FCSTD DOCUMENT  (FreeCAD 0.20R29410 (Git))
Label: copter
License: All rights reserved
LicenseURL: http://en.wikipedia.org/wiki/All_rights_reserved
objects: App::Link×23, App::DocumentObjectGroup×3, PartDesign::CoordinateSystem×1, App::FeaturePython×1, App::Part×1
note: 1 computed .brp shape members not serialized (recipe doc carries the construction recipe); baked Part::Feature solids carry a one-line shape summary decoded from their .brp
EXTERNAL_REF file=lower_plate.FCStd obj=LCS_1
EXTERNAL_REF file=lower_plate.FCStd obj=Body
EXTERNAL_REF file=arm.FCStd obj=LCS_IR
EXTERNAL_REF file=lower_plate.FCStd obj=LCS_7
EXTERNAL_REF file=arm.FCStd obj=Body
EXTERNAL_REF file=arm.FCStd obj=LCS_IL
EXTERNAL_REF file=lower_plate.FCStd obj=LCS_6
EXTERNAL_REF file=lower_plate.FCStd obj=LCS_2
EXTERNAL_REF file=lower_plate.FCStd obj=LCS_3
EXTERNAL_REF file=arm.FCStd obj=LCS_1
EXTERNAL_REF file=motor_1810.FCStd obj=LCS_1
EXTERNAL_REF file=motor_1810.FCStd obj=Body
EXTERNAL_REF file=arm.FCStd obj=LCS_R
EXTERNAL_REF file=middle_plate.FCStd obj=LCS_1
EXTERNAL_REF file=middle_plate.FCStd obj=Body
EXTERNAL_REF file=back_pillar.FCStd obj=LCS_1
EXTERNAL_REF file=lower_plate.FCStd obj=LCS_4
EXTERNAL_REF file=back_pillar.FCStd obj=Body
EXTERNAL_REF file=lower_plate.FCStd obj=LCS_5
EXTERNAL_REF file=back_pillar.FCStd obj=LCS_2
EXTERNAL_REF file=top_plate.FCStd obj=LCS_2
EXTERNAL_REF file=top_plate.FCStd obj=Body
EXTERNAL_REF file=front_pillar.FCStd obj=LCS_1
EXTERNAL_REF file=middle_plate.FCStd obj=LCS_2
EXTERNAL_REF file=front_pillar.FCStd obj=Body
EXTERNAL_REF file=middle_plate.FCStd obj=LCS_3
EXTERNAL_REF file=prop.FCStd obj=Body
EXTERNAL_REF file=prop1.FCStd obj=Body001
EXTERNAL_REF file=lower_plate.FCStd obj=LCS_8
EXTERNAL_REF file=lower_plate.FCStd obj=LCS_9
EXTERNAL_REF file=middle_plate.FCStd obj=LCS_4
EXTERNAL_REF file=middle_plate.FCStd obj=LCS_5

FEATURE [App::DocumentObjectGroup] Parts
FEATURE [PartDesign::CoordinateSystem] LCS_Origin
  AttacherType = Attacher::AttachEngine3D
  MapMode = 2
  Support = -> [X_Axis]
FEATURE [App::DocumentObjectGroup] Constraints
FEATURE [App::FeaturePython] Variables  # WARN: FeaturePython — macro-defined, semantics opaque (R4)
  Type = App::PropertyContainer
  angle = 720
  minus_angle = 180
FEATURE [App::DocumentObjectGroup] Configurations
FEATURE [App::Link] Body  label="LowerPlate"
  AssemblyType = Part::Link
  AttachedBy = #LCS_1
  AttachedTo = Parent Assembly#LCS_Origin
  LinkPlacement = pos=(-17.5,100,0) rot=(0,0,1;0rad)
  LinkedObject = -> <external lower_plate.FCStd>#Body
  Placement = pos=(-17.5,100,0) rot=(0,0,1;0rad)
  SolverId = Asm4EE
  expr: Placement = LCS_Origin.Placement * AttachmentOffset * lower_plate#LCS_1.Placement ^ -1
FEATURE [App::Link] Body001  label="Arm1"
  AssemblyType = Part::Link
  AttachedBy = #LCS_IR
  AttachedTo = Body#LCS_7
  LinkPlacement = pos=(-17.75,100.25,2) rot=(0,0,1;0rad)
  LinkedObject = -> <external arm.FCStd>#Body
  Placement = pos=(-17.75,100.25,2) rot=(0,0,1;0rad)
  SolverId = Asm4EE
  expr: Placement = Body.Placement * lower_plate#LCS_7.Placement * AttachmentOffset * arm#LCS_IR.Placement ^ -1
FEATURE [App::Link] Body_2  label="Arm4"
  AssemblyType = Part::Link
  AttachedBy = #LCS_IL
  AttachedTo = Body#LCS_6
  AttachmentOffset = pos=(0,0,0) rot=(1,0,0;3.14159rad)
  LinkPlacement = pos=(-17.25,100.25,6) rot=(0,1,0;3.14159rad)
  LinkedObject = -> <external arm.FCStd>#Body
  Placement = pos=(-17.25,100.25,6) rot=(0,1,0;3.14159rad)
  SolverId = Asm4EE
  expr: Placement = Body.Placement * lower_plate#LCS_6.Placement * AttachmentOffset * arm#LCS_IL.Placement ^ -1
FEATURE [App::Link] Body002  label="Arm2"
  AssemblyType = Part::Link
  AttachedBy = #LCS_IL
  AttachedTo = Body#LCS_2
  AttachmentOffset = pos=(0,0,0) rot=(0,1,0;3.14159rad)
  LinkPlacement = pos=(-17.75,99.75,6) rot=(-1,0,0;3.14159rad)
  LinkedObject = -> <external arm.FCStd>#Body
  Placement = pos=(-17.75,99.75,6) rot=(-1,0,0;3.14159rad)
  SolverId = Asm4EE
  expr: Placement = Body.Placement * lower_plate#LCS_2.Placement * AttachmentOffset * arm#LCS_IL.Placement ^ -1
FEATURE [App::Link] Body003  label="Arm3"
  AssemblyType = Part::Link
  AttachedBy = #LCS_IR
  AttachedTo = Body#LCS_3
  AttachmentOffset = pos=(0,0,0) rot=(0,0,1;3.14159rad)
  LinkPlacement = pos=(-17.25,99.75,2) rot=(0,0,1;3.14159rad)
  LinkedObject = -> <external arm.FCStd>#Body
  Placement = pos=(-17.25,99.75,2) rot=(0,0,1;3.14159rad)
  SolverId = Asm4EE
  expr: Placement = Body.Placement * lower_plate#LCS_3.Placement * AttachmentOffset * arm#LCS_IR.Placement ^ -1
FEATURE [App::Link] Body004  label="Motor1"
  AssemblyType = Part::Link
  AttachedBy = #LCS_1
  AttachedTo = Body001#LCS_1
  AttachmentOffset = pos=(0,0,0) rot=(1,0,0;3.14159rad)
  LinkPlacement = pos=(-113.703,173.838,6) rot=(0,0,1;4.01426rad)
  LinkedObject = -> <external motor_1810.FCStd>#Body
  Placement = pos=(-113.703,173.838,6) rot=(0,0,1;4.01426rad)
  SolverId = Asm4EE
  expr: .Placement.Rotation.Angle = 230
  expr: Placement = Body001.Placement * arm#LCS_1.Placement * AttachmentOffset * motor_1810#LCS_1.Placement ^ -1
FEATURE [App::Link] Body006  label="Motor2"
  AssemblyType = Part::Link
  AttachedBy = #LCS_1
  AttachedTo = Body002#LCS_R
  LinkPlacement = pos=(-113.703,26.162,6) rot=(0,0,1;5.41052rad)
  LinkedObject = -> <external motor_1810.FCStd>#Body
  Placement = pos=(-113.703,26.162,6) rot=(0,0,1;5.41052rad)
  SolverId = Asm4EE
  expr: .Placement.Rotation.Angle = 300
  expr: Placement = Body002.Placement * arm#LCS_R.Placement * AttachmentOffset * motor_1810#LCS_1.Placement ^ -1
FEATURE [App::Link] Body007  label="Motor3"
  AssemblyType = Part::Link
  AttachedBy = #LCS_1
  AttachedTo = Body003#LCS_1
  AttachmentOffset = pos=(0,0,0) rot=(1,0,0;3.14159rad)
  LinkPlacement = pos=(78.703,26.162,6) rot=(0,0,-1;5.41052rad)
  LinkedObject = -> <external motor_1810.FCStd>#Body
  Placement = pos=(78.703,26.162,6) rot=(0,0,-1;5.41052rad)
  SolverId = Asm4EE
  expr: .Placement.Rotation.Angle = 60
  expr: Placement = Body003.Placement * arm#LCS_1.Placement * AttachmentOffset * motor_1810#LCS_1.Placement ^ -1
FEATURE [App::Link] Body008  label="Motor4"
  AssemblyType = Part::Link
  AttachedBy = #LCS_1
  AttachedTo = Body_2#LCS_R
  LinkPlacement = pos=(78.703,173.838,6) rot=(0,0,1;2.26893rad)
  LinkedObject = -> <external motor_1810.FCStd>#Body
  Placement = pos=(78.703,173.838,6) rot=(0,0,1;2.26893rad)
  SolverId = Asm4EE
  expr: .Placement.Rotation.Angle = 120
  expr: Placement = Body_2.Placement * arm#LCS_R.Placement * AttachmentOffset * motor_1810#LCS_1.Placement ^ -1
FEATURE [App::Link] Body001006  label="MiddlePlate"
  AssemblyType = Part::Link
  AttachedBy = #LCS_1
  AttachedTo = Body_2#LCS_IR
  AttachmentOffset = pos=(0,0,0) rot=(1,0,0;3.14159rad)
  LinkPlacement = pos=(-17.5,100,6) rot=(0,0,1;0rad)
  LinkedObject = -> <external middle_plate.FCStd>#Body
  Placement = pos=(-17.5,100,6) rot=(0,0,1;0rad)
  SolverId = Asm4EE
  expr: Placement = Body_2.Placement * arm#LCS_IR.Placement * AttachmentOffset * middle_plate#LCS_1.Placement ^ -1
FEATURE [App::Link] Body001007  label="BackPillarLeft"
  AssemblyType = Part::Link
  AttachedBy = #LCS_1
  AttachedTo = Body#LCS_4
  LinkPlacement = pos=(-31,4,2) rot=(0,0,1;0rad)
  LinkedObject = -> <external back_pillar.FCStd>#Body
  Placement = pos=(-31,4,2) rot=(0,0,1;0rad)
  SolverId = Asm4EE
  expr: Placement = Body.Placement * lower_plate#LCS_4.Placement * AttachmentOffset * back_pillar#LCS_1.Placement ^ -1
FEATURE [App::Link] Body001008  label="BackPillarRight"
  AssemblyType = Part::Link
  AttachedBy = #LCS_1
  AttachedTo = Body#LCS_5
  LinkPlacement = pos=(-4,4,2) rot=(0,0,1;0rad)
  LinkedObject = -> <external back_pillar.FCStd>#Body
  Placement = pos=(-4,4,2) rot=(0,0,1;0rad)
  SolverId = Asm4EE
  expr: Placement = Body.Placement * lower_plate#LCS_5.Placement * AttachmentOffset * back_pillar#LCS_1.Placement ^ -1
FEATURE [App::Link] Body001009  label="TopPlate"
  AssemblyType = Part::Link
  AttachedBy = #LCS_2
  AttachedTo = Body001007#LCS_2
  AttachmentOffset = pos=(0,0,0) rot=(0,0,1;3.14159rad)
  LinkPlacement = pos=(-17.5,100,37) rot=(0,0,1;3.14159rad)
  LinkedObject = -> <external top_plate.FCStd>#Body
  Placement = pos=(-17.5,100,37) rot=(0,0,1;3.14159rad)
  SolverId = Asm4EE
  expr: Placement = Body001007.Placement * back_pillar#LCS_2.Placement * AttachmentOffset * top_plate#LCS_2.Placement ^ -1
FEATURE [App::Link] Body001010  label="FrontPillarLeft"
  AssemblyType = Part::Link
  AttachedBy = #LCS_1
  AttachedTo = Body001006#LCS_2
  LinkPlacement = pos=(-31,196,8) rot=(0,0,1;0rad)
  LinkedObject = -> <external front_pillar.FCStd>#Body
  Placement = pos=(-31,196,8) rot=(0,0,1;0rad)
  SolverId = Asm4EE
  expr: Placement = Body001006.Placement * middle_plate#LCS_2.Placement * AttachmentOffset * front_pillar#LCS_1.Placement ^ -1
FEATURE [App::Link] Body001011  label="FrontPillarRight"
  AssemblyType = Part::Link
  AttachedBy = #LCS_1
  AttachedTo = Body001006#LCS_3
  LinkPlacement = pos=(-4,196,8) rot=(0,0,1;0rad)
  LinkedObject = -> <external front_pillar.FCStd>#Body
  Placement = pos=(-4,196,8) rot=(0,0,1;0rad)
  SolverId = Asm4EE
  expr: Placement = Body001006.Placement * middle_plate#LCS_3.Placement * AttachmentOffset * front_pillar#LCS_1.Placement ^ -1
FEATURE [App::Link] Body001012  label="Prop1"
  AssemblyType = Part::Link
  AttachedBy = #LCS_1
  AttachedTo = Body004#LCS_2
  AttachmentOffset = pos=(0,0,0) rot=(1,0,0;3.14159rad)
  LinkPlacement = pos=(-113.453,173.588,27.3) rot=(0,0,1;12.5664rad)
  LinkedObject = -> <external prop.FCStd>#Body
  Placement = pos=(-113.453,173.588,27.3) rot=(0,0,1;12.5664rad)
  SolverId = Asm4EE
  expr: .Placement.Rotation.Angle = Variables.angle
FEATURE [App::Link] Body001013  label="Prop2"
  AssemblyType = Part::Link
  AttachedBy = #LCS_2
  AttachedTo = Body006#LCS_2
  AttachmentOffset = pos=(0,0,0) rot=(0,0,1;3.14159rad)
  LinkPlacement = pos=(-113.453,26.412,27.3) rot=(0,0,1;-12.5664rad)
  LinkedObject = -> <external prop1.FCStd>#Body001
  Placement = pos=(-113.453,26.412,27.3) rot=(0,0,1;-12.5664rad)
  SolverId = Asm4EE
  expr: .Placement.Rotation.Angle = -Variables.angle
FEATURE [App::Link] Body001014  label="Prop3"
  AssemblyType = Part::Link
  AttachedBy = #LCS_1
  AttachedTo = Body007#LCS_2
  AttachmentOffset = pos=(0,0,0) rot=(0.707107,-0.707107,0;3.14159rad)
  LinkPlacement = pos=(78.453,26.412,27.3) rot=(0,0,1;12.5664rad)
  LinkedObject = -> <external prop.FCStd>#Body
  Placement = pos=(78.453,26.412,27.3) rot=(0,0,1;12.5664rad)
  SolverId = Asm4EE
  expr: .Placement.Rotation.Angle = Variables.angle
FEATURE [App::Link] Body001015  label="Prop4"
  AssemblyType = Part::Link
  AttachedBy = #LCS_2
  AttachedTo = Body008#LCS_2
  AttachmentOffset = pos=(0,0,0) rot=(0,0,1;3.14159rad)
  LinkPlacement = pos=(78.453,173.588,27.3) rot=(0,0,1;-12.5664rad)
  LinkedObject = -> <external prop1.FCStd>#Body001
  Placement = pos=(78.453,173.588,27.3) rot=(0,0,1;-12.5664rad)
  SolverId = Asm4EE
  expr: .Placement.Rotation.Angle = -Variables.angle
FEATURE [App::Link] Body001016  label="BackPIllarMidLeft"
  AssemblyType = Part::Link
  AttachedBy = #LCS_1
  AttachedTo = Body#LCS_8
  LinkPlacement = pos=(-31,70,2) rot=(0,0,1;0rad)
  LinkedObject = -> <external back_pillar.FCStd>#Body
  Placement = pos=(-31,70,2) rot=(0,0,1;0rad)
  SolverId = Asm4EE
  expr: Placement = Body.Placement * lower_plate#LCS_8.Placement * AttachmentOffset * back_pillar#LCS_1.Placement ^ -1
FEATURE [App::Link] Body001017  label="BackPillarMiddleRight"
  AssemblyType = Part::Link
  AttachedBy = #LCS_1
  AttachedTo = Body#LCS_9
  LinkPlacement = pos=(-4,70,2) rot=(0,0,1;0rad)
  LinkedObject = -> <external back_pillar.FCStd>#Body
  Placement = pos=(-4,70,2) rot=(0,0,1;0rad)
  SolverId = Asm4EE
  expr: Placement = Body.Placement * lower_plate#LCS_9.Placement * AttachmentOffset * back_pillar#LCS_1.Placement ^ -1
FEATURE [App::Link] Body001018  label="FrontPillarMidLeft"
  AssemblyType = Part::Link
  AttachedBy = #LCS_1
  AttachedTo = Body001006#LCS_4
  LinkPlacement = pos=(-31,140,8) rot=(0,0,1;0rad)
  LinkedObject = -> <external front_pillar.FCStd>#Body
  Placement = pos=(-31,140,8) rot=(0,0,1;0rad)
  SolverId = Asm4EE
  expr: Placement = Body001006.Placement * middle_plate#LCS_4.Placement * AttachmentOffset * front_pillar#LCS_1.Placement ^ -1
FEATURE [App::Link] Body_3  label="FronPillarMidRight"
  AssemblyType = Part::Link
  AttachedBy = #LCS_1
  AttachedTo = Body001006#LCS_5
  LinkPlacement = pos=(-4,140,8) rot=(0,0,1;0rad)
  LinkedObject = -> <external front_pillar.FCStd>#Body
  Placement = pos=(-4,140,8) rot=(0,0,1;0rad)
  SolverId = Asm4EE
  expr: Placement = Body001006.Placement * middle_plate#LCS_5.Placement * AttachmentOffset * front_pillar#LCS_1.Placement ^ -1
FEATURE [App::Part] Model
  AssemblyType = Part::Link
  Group = -> [LCS_Origin,Constraints,Variables,Configurations,Body,Body001,Body_2,Body002,Body003,Body004,Body006,Body007,Body008,Body001006,Body001007,Body001008,Body001009,Body001010,Body001011,Body001012,Body001013,Body001014,Body001015,Body001016,Body001017,Body001018,Body_3]
  Origin = -> Origin
  Type = Assembly

RESOLVED EXTERNAL PARTS (link-assembly join: the EXTERNAL_REF files above that resolve inside this repo's crawl, each included once):
---- part arm.FCStd = doc fcstd_1915403416bb ----
FCSTD DOCUMENT  (FreeCAD 0.20R29410 (Git))
Label: arm
License: All rights reserved
LicenseURL: http://en.wikipedia.org/wiki/All_rights_reserved
objects: PartDesign::CoordinateSystem×4, Sketcher::SketchObject×1, PartDesign::Pad×1, PartDesign::Body×1
note: 8 computed .brp shape members not serialized (recipe doc carries the construction recipe); baked Part::Feature solids carry a one-line shape summary decoded from their .brp

FEATURE [Sketcher::SketchObject] Sketch
  FullyConstrained = true
  MapMode = 5
  Support = -> [XY_Plane]
  sketch-geometry (22):
    g0: LineSegment StartX=-20 StartY=0 StartZ=0 EndX=0 EndY=0 EndZ=0
    g1: LineSegment StartX=0 StartY=0 StartZ=0 EndX=0 EndY=15 EndZ=0
    g2: LineSegment StartX=-20 StartY=0 StartZ=0 EndX=-96.6044 EndY=64.2788 EndZ=0
    g3: LineSegment StartX=0 StartY=15 StartZ=0 EndX=-86.8979 EndY=75.8466 EndZ=0
    g4: LineSegment StartX=-96.6044 StartY=64.2788 StartZ=0 EndX=-86.8979 EndY=75.8466 EndZ=0
    g5: LineSegment StartX=-91.7514 StartY=70.0624 StartZ=0 EndX=-95.0006 EndY=78.9895 EndZ=0
    g6: LineSegment StartX=-95.0006 StartY=78.9895 StartZ=0 EndX=-101.107 EndY=71.7121 EndZ=0
    g7: LineSegment StartX=-101.107 StartY=71.7121 StartZ=0 EndX=-91.7514 EndY=70.0624 EndZ=0
    g8: Circle CenterX=-95.953 CenterY=73.588 CenterZ=0 NormalX=0 NormalY=0 NormalZ=1 AngleXU=0 Radius=5.48483
    g9: Circle CenterX=-91.7514 CenterY=70.0624 CenterZ=0 NormalX=0 NormalY=0 NormalZ=1 AngleXU=0 Radius=1.1
    g10: Circle CenterX=-95.0006 CenterY=78.9895 CenterZ=0 NormalX=0 NormalY=0 NormalZ=1 AngleXU=0 Radius=1.1
    g11: Circle CenterX=-101.107 CenterY=71.7121 CenterZ=0 NormalX=0 NormalY=0 NormalZ=1 AngleXU=0 Radius=1.1
    g12: ArcOfCircle CenterX=-95.953 CenterY=73.588 CenterZ=0 NormalX=0 NormalY=0 NormalZ=1 AngleXU=0 Radius=3.75 StartAngle=1.79996 EndAngle=3.08696
    g13: ArcOfCircle CenterX=-95.0006 CenterY=78.9895 CenterZ=0 NormalX=0 NormalY=0 NormalZ=1 AngleXU=0 Radius=2 StartAngle=0.311549 EndAngle=3.45314
    g14: ArcOfCircle CenterX=-101.107 CenterY=71.7121 CenterZ=0 NormalX=0 NormalY=0 NormalZ=1 AngleXU=0 Radius=2 StartAngle=1.43378 EndAngle=4.57537
    g15: LineSegment StartX=-96.8049 StartY=77.2399 StartZ=0 EndX=-96.9043 EndY=78.3764 EndZ=0
    g16: LineSegment StartX=-99.6974 StartY=73.7927 StartZ=0 EndX=-100.834 EndY=73.6933 EndZ=0
    g17: LineSegment StartX=-99.6974 StartY=73.7927 StartZ=0 EndX=-96.8049 EndY=77.2399 EndZ=0
    g18: LineSegment StartX=-86.8979 StartY=75.8466 StartZ=0 EndX=-93.0969 EndY=79.6025 EndZ=0
    g19: LineSegment StartX=-96.6044 StartY=64.2788 StartZ=0 EndX=-101.38 EndY=69.7308 EndZ=0
    g20: Circle CenterX=-95.953 CenterY=73.588 CenterZ=0 NormalX=0 NormalY=0 NormalZ=1 AngleXU=0 Radius=2.25
    g21: Circle CenterX=-15 CenterY=15 CenterZ=0 NormalX=0 NormalY=0 NormalZ=1 AngleXU=0 Radius=1.55
  constraints (59):
    c: PointOnObject(g0,g-1)
    c: Coincident(g0,g-1)
    c: Coincident(g1,g0)
    c: PointOnObject(g1,g-2)
    c: Coincident(g2,g0)
    c: Coincident(g3,g1)
    c: DistanceY(g1,g1) = 15
    c: DistanceX(g0,g0) = 20
    c: Angle(g-1,g2) = 2.44346
    c: Coincident(g4,g2)
    c: Coincident(g4,g3)
    c: Angle(g2,g4) = 1.5708
    c: Angle(g2,g3) = 0.0872665
    c: Distance(g2) = 100
    c: Coincident(g5,g6)
    c: Coincident(g6,g7)
    c: Coincident(g7,g5)
    c: Equal(g5,g6)
    c: Equal(g5,g7)
    c: PointOnObject(g5,g8)
    c: PointOnObject(g6,g8)
    c: PointOnObject(g7,g8)
    c: PointOnObject(g5,g4)
    c: Parallel(g6,g4)
    c: Distance(g5,g2) = 7.55
    c: Coincident(g9,g5)
    c: Coincident(g10,g5)
    c: Coincident(g11,g6)
    c: Equal(g10,g11)
    c: Equal(g10,g9)
    c: Diameter(g10) = 2.2
    c: Distance(g7) = 9.5
    c: Coincident(g12,g8)
    c: Diameter(g12) = 7.5
    c: Coincident(g13,g10)
    c: Coincident(g14,g11)
    c: Diameter(g14) = 4
    c: Diameter(g13) = 4
    c: Angle(g14) = 3.14159
    c: Angle(g13) = 3.14159
    c: Coincident(g15,g12)
    c: Coincident(g15,g13)
    c: Coincident(g16,g12)
    c: Coincident(g16,g14)
    c: Angle(g15,g16) = 1.5708
    c: Equal(g16,g15)
    c: Coincident(g17,g12)
    c: Coincident(g17,g12)
    c: Parallel(g17,g4)
    c: Distance(g17) = 4.5
    c: Coincident(g18,g3)
    c: Coincident(g18,g13)
    c: Coincident(g19,g2)
    c: Coincident(g19,g14)
    c: Coincident(g20,g12)
    c: Diameter(g20) = 4.5
    c: Diameter(g21) = 3.1
    c: DistanceX(g21,g0) = 15
    c: DistanceY(g0,g21) = 15
FEATURE [PartDesign::Pad] Pad
  Direction = (0,0,1)
  Length = 4
  Length2 = 10
  Profile = -> Sketch
  ReferenceAxis = -> Sketch [N_Axis]
  Type = 0
FEATURE [PartDesign::CoordinateSystem] LCS_1  label="LCS_L"
  AttacherType = Attacher::AttachEngine3D
  AttachmentOffset = pos=(0,0,0) rot=(0,0,1;0.872665rad)
  MapMode = 11
  Placement = pos=(-95.953,73.588,4) rot=(0,0,1;2.44346rad)
  Support = -> [Pad]
FEATURE [PartDesign::CoordinateSystem] LCS_R
  AttacherType = Attacher::AttachEngine3D
  AttachmentOffset = pos=(0,0,0) rot=(0,0,1;0.872665rad)
  MapMode = 11
  Placement = pos=(-95.953,73.588,0) rot=(0,0,1;2.44346rad)
  Support = -> [Pad]
FEATURE [PartDesign::CoordinateSystem] LCS_IL
  AttacherType = Attacher::AttachEngine3D
  MapMode = 11
  Placement = pos=(-15,15,4) rot=(0,0,1;1.5708rad)
  Support = -> [Pad]
FEATURE [PartDesign::CoordinateSystem] LCS_IR
  AttacherType = Attacher::AttachEngine3D
  MapMode = 11
  Placement = pos=(-15,15,0) rot=(0,0,1;1.5708rad)
  Support = -> [Pad]
FEATURE [PartDesign::Body] Body
  Group = -> [Sketch,Pad,LCS_1,LCS_R,LCS_IL,LCS_IR]
  Origin = -> Origin
  Tip = -> Pad
---- part back_pillar.FCStd = doc fcstd_aa81737c5687 ----
FCSTD DOCUMENT  (FreeCAD 0.20R29410 (Git))
Label: back_pillar
License: All rights reserved
LicenseURL: http://en.wikipedia.org/wiki/All_rights_reserved
objects: PartDesign::CoordinateSystem×2, Sketcher::SketchObject×1, PartDesign::Pad×1, PartDesign::Body×1
note: 6 computed .brp shape members not serialized (recipe doc carries the construction recipe); baked Part::Feature solids carry a one-line shape summary decoded from their .brp

FEATURE [Sketcher::SketchObject] Sketch
  FullyConstrained = true
  MapMode = 5
  Support = -> [XY_Plane]
  sketch-geometry (2):
    g0: Circle CenterX=0 CenterY=0 CenterZ=0 NormalX=0 NormalY=0 NormalZ=1 AngleXU=0 Radius=2.5
    g1: Circle CenterX=0 CenterY=0 CenterZ=0 NormalX=0 NormalY=0 NormalZ=1 AngleXU=0 Radius=1.5
  constraints (4):
    c: Coincident(g0,g-1)
    c: Coincident(g1,g0)
    c: Diameter(g0) = 5
    c: Diameter(g1) = 3
FEATURE [PartDesign::Pad] Pad
  Direction = (0,0,1)
  Length = 35
  Length2 = 10
  Profile = -> Sketch
  ReferenceAxis = -> Sketch [N_Axis]
  Type = 0
FEATURE [PartDesign::CoordinateSystem] LCS_1
  AttacherType = Attacher::AttachEngine3D
  MapMode = 11
  Placement = pos=(0,0,0) rot=(0,0,1;1.5708rad)
  Support = -> [Pad]
FEATURE [PartDesign::CoordinateSystem] LCS_2
  AttacherType = Attacher::AttachEngine3D
  MapMode = 11
  Placement = pos=(0,0,35) rot=(0,0,1;1.5708rad)
  Support = -> [Pad]
FEATURE [PartDesign::Body] Body
  Group = -> [Sketch,Pad,LCS_1,LCS_2]
  Origin = -> Origin
  Tip = -> Pad
---- part front_pillar.FCStd = doc fcstd_1f7aed564d2c ----
FCSTD DOCUMENT  (FreeCAD 0.20R29410 (Git))
Label: front_pillar
License: All rights reserved
LicenseURL: http://en.wikipedia.org/wiki/All_rights_reserved
objects: PartDesign::CoordinateSystem×2, Sketcher::SketchObject×1, PartDesign::Pad×1, PartDesign::Body×1
note: 6 computed .brp shape members not serialized (recipe doc carries the construction recipe); baked Part::Feature solids carry a one-line shape summary decoded from their .brp

FEATURE [Sketcher::SketchObject] Sketch
  FullyConstrained = true
  MapMode = 5
  Support = -> [XY_Plane]
  sketch-geometry (2):
    g0: Circle CenterX=0 CenterY=0 CenterZ=0 NormalX=0 NormalY=0 NormalZ=1 AngleXU=0 Radius=2.5
    g1: Circle CenterX=0 CenterY=0 CenterZ=0 NormalX=0 NormalY=0 NormalZ=1 AngleXU=0 Radius=1.55
  constraints (4):
    c: Coincident(g0,g-1)
    c: Coincident(g1,g0)
    c: Diameter(g1) = 3.1
    c: Diameter(g0) = 5
FEATURE [PartDesign::Pad] Pad
  Direction = (0,0,1)
  Length = 29
  Length2 = 10
  Profile = -> Sketch
  ReferenceAxis = -> Sketch [N_Axis]
  Type = 0
FEATURE [PartDesign::CoordinateSystem] LCS_1
  AttacherType = Attacher::AttachEngine3D
  MapMode = 11
  Placement = pos=(0,0,0) rot=(0,0,1;1.5708rad)
  Support = -> [Pad]
FEATURE [PartDesign::CoordinateSystem] LCS_2
  AttacherType = Attacher::AttachEngine3D
  MapMode = 11
  Placement = pos=(0,0,29) rot=(0,0,1;1.5708rad)
  Support = -> [Pad]
FEATURE [PartDesign::Body] Body
  Group = -> [Sketch,Pad,LCS_1,LCS_2]
  Origin = -> Origin
  Tip = -> Pad
---- part lower_plate.FCStd = doc fcstd_91a2898a4a48 ----
FCSTD DOCUMENT  (FreeCAD 0.20R29410 (Git))
Label: lower_plate
License: All rights reserved
LicenseURL: http://en.wikipedia.org/wiki/All_rights_reserved
objects: PartDesign::CoordinateSystem×9, Sketcher::SketchObject×1, PartDesign::Pad×1, PartDesign::Body×1
note: 13 computed .brp shape members not serialized (recipe doc carries the construction recipe); baked Part::Feature solids carry a one-line shape summary decoded from their .brp

FEATURE [Sketcher::SketchObject] Sketch
  FullyConstrained = true
  MapMode = 5
  Support = -> [XY_Plane]
  sketch-geometry (12):
    g0: LineSegment StartX=-17.5 StartY=20 StartZ=0 EndX=17.5 EndY=20 EndZ=0
    g1: LineSegment StartX=17.5 StartY=20 StartZ=0 EndX=17.5 EndY=-100 EndZ=0
    g2: LineSegment StartX=-17.5 StartY=-100 StartZ=0 EndX=-17.5 EndY=20 EndZ=0
    g3: Circle CenterX=-15.25 CenterY=15.25 CenterZ=0 NormalX=0 NormalY=0 NormalZ=1 AngleXU=0 Radius=1.55
    g4: Circle CenterX=15.25 CenterY=15.25 CenterZ=0 NormalX=0 NormalY=0 NormalZ=1 AngleXU=0 Radius=1.55
    g5: Circle CenterX=-15.25 CenterY=-15.25 CenterZ=0 NormalX=0 NormalY=0 NormalZ=1 AngleXU=0 Radius=1.55
    g6: Circle CenterX=15.25 CenterY=-15.25 CenterZ=0 NormalX=0 NormalY=0 NormalZ=1 AngleXU=0 Radius=1.55
    g7: LineSegment StartX=-17.5 StartY=-100 StartZ=0 EndX=17.5 EndY=-100 EndZ=0
    g8: Circle CenterX=-13.5 CenterY=-96 CenterZ=0 NormalX=0 NormalY=0 NormalZ=1 AngleXU=0 Radius=1.55
    g9: Circle CenterX=13.5 CenterY=-96 CenterZ=0 NormalX=0 NormalY=0 NormalZ=1 AngleXU=0 Radius=1.55
    g10: Circle CenterX=-13.5 CenterY=-30 CenterZ=0 NormalX=0 NormalY=0 NormalZ=1 AngleXU=0 Radius=1.55
    g11: Circle CenterX=13.5 CenterY=-30 CenterZ=0 NormalX=0 NormalY=0 NormalZ=1 AngleXU=0 Radius=1.55
  constraints (30):
    c: Coincident(g0,g1)
    c: Coincident(g2,g0)
    c: Vertical(g2)
    c: DistanceX(g2,g1) = 35
    c: Equal(g6,g5)
    c: Equal(g5,g3)
    c: Equal(g3,g4)
    c: Symmetric(g3,g4,g-2)
    c: Symmetric(g6,g4,g-1)
    c: Symmetric(g3,g5,g-1)
    c: DistanceX(g3,g4) = 30.5
    c: DistanceY(g6,g4) = 30.5
    c: Diameter(g6) = 3.1
    c: Vertical(g1)
    c: DistanceY(g-1,g0) = 20
    c: Symmetric(g0,g0,g-2)
    c: Equal(g2,g1)
    c: DistanceY(g1,g1) = 120
    c: Coincident(g7,g2)
    c: Coincident(g7,g1)
    c: Equal(g9,g8)
    c: Diameter(g9) = 3.1
    c: Symmetric(g8,g9,g-2)
    c: DistanceX(g9,g1) = 4
    c: DistanceY(g1,g9) = 4
    c: Equal(g11,g10)
    c: Symmetric(g11,g10,g-2)
    c: Diameter(g11) = 3.1
    c: DistanceX(g11,g1) = 4
    c: DistanceY(g1,g11) = 70
FEATURE [PartDesign::Pad] Pad
  Direction = (0,0,1)
  Length = 2
  Length2 = 10
  Profile = -> Sketch
  ReferenceAxis = -> Sketch [N_Axis]
  Type = 0
FEATURE [PartDesign::CoordinateSystem] LCS_1
  AttacherType = Attacher::AttachEngine3D
  MapMode = 1
  Placement = pos=(17.5,-100,0) rot=(0,0,1;0rad)
  Support = -> [Pad]
FEATURE [PartDesign::CoordinateSystem] LCS_2
  AttacherType = Attacher::AttachEngine3D
  MapMode = 11
  Placement = pos=(-15.25,-15.25,2) rot=(0,0,1;1.5708rad)
  Support = -> [Pad]
FEATURE [PartDesign::CoordinateSystem] LCS_3
  AttacherType = Attacher::AttachEngine3D
  MapMode = 11
  Placement = pos=(15.25,-15.25,2) rot=(0,0,1;1.5708rad)
  Support = -> [Pad]
FEATURE [PartDesign::CoordinateSystem] LCS_4
  AttacherType = Attacher::AttachEngine3D
  MapMode = 11
  Placement = pos=(-13.5,-96,2) rot=(0,0,1;1.5708rad)
  Support = -> [Pad]
FEATURE [PartDesign::CoordinateSystem] LCS_5
  AttacherType = Attacher::AttachEngine3D
  MapMode = 11
  Placement = pos=(13.5,-96,2) rot=(0,0,1;1.5708rad)
  Support = -> [Pad]
FEATURE [PartDesign::CoordinateSystem] LCS_6
  AttacherType = Attacher::AttachEngine3D
  MapMode = 11
  Placement = pos=(15.25,15.25,2) rot=(0,0,1;1.5708rad)
  Support = -> [Pad]
FEATURE [PartDesign::CoordinateSystem] LCS_7
  AttacherType = Attacher::AttachEngine3D
  MapMode = 11
  Placement = pos=(-15.25,15.25,2) rot=(0,0,1;1.5708rad)
  Support = -> [Pad]
FEATURE [PartDesign::CoordinateSystem] LCS_8
  AttacherType = Attacher::AttachEngine3D
  MapMode = 11
  Placement = pos=(-13.5,-30,2) rot=(0,0,1;1.5708rad)
  Support = -> [Pad]
FEATURE [PartDesign::CoordinateSystem] LCS_9
  AttacherType = Attacher::AttachEngine3D
  MapMode = 11
  Placement = pos=(13.5,-30,2) rot=(0,0,1;1.5708rad)
  Support = -> [Pad]
FEATURE [PartDesign::Body] Body
  Group = -> [Sketch,Pad,LCS_1,LCS_2,LCS_3,LCS_4,LCS_5,LCS_6,LCS_7,LCS_8,LCS_9]
  Origin = -> Origin
  Tip = -> Pad
---- part middle_plate.FCStd = doc fcstd_eb9f5ccd6ca6 ----
FCSTD DOCUMENT  (FreeCAD 0.20R29410 (Git))
Label: middle_plate
License: All rights reserved
LicenseURL: http://en.wikipedia.org/wiki/All_rights_reserved
objects: PartDesign::CoordinateSystem×5, Sketcher::SketchObject×1, PartDesign::Pad×1, PartDesign::Body×1
note: 9 computed .brp shape members not serialized (recipe doc carries the construction recipe); baked Part::Feature solids carry a one-line shape summary decoded from their .brp

FEATURE [Sketcher::SketchObject] Sketch
  FullyConstrained = true
  MapMode = 5
  Support = -> [XY_Plane]
  sketch-geometry (12):
    g0: LineSegment StartX=-17.5 StartY=100 StartZ=0 EndX=17.5 EndY=100 EndZ=0
    g1: LineSegment StartX=17.5 StartY=100 StartZ=0 EndX=17.5 EndY=-20 EndZ=0
    g2: LineSegment StartX=17.5 StartY=-20 StartZ=0 EndX=-17.5 EndY=-20 EndZ=0
    g3: LineSegment StartX=-17.5 StartY=-20 StartZ=0 EndX=-17.5 EndY=100 EndZ=0
    g4: Circle CenterX=-15.25 CenterY=15.25 CenterZ=0 NormalX=0 NormalY=0 NormalZ=1 AngleXU=0 Radius=1.55
    g5: Circle CenterX=15.25 CenterY=15.25 CenterZ=0 NormalX=0 NormalY=0 NormalZ=1 AngleXU=0 Radius=1.55
    g6: Circle CenterX=-15.25 CenterY=-15.25 CenterZ=0 NormalX=0 NormalY=0 NormalZ=1 AngleXU=0 Radius=1.55
    g7: Circle CenterX=15.25 CenterY=-15.25 CenterZ=0 NormalX=0 NormalY=0 NormalZ=1 AngleXU=0 Radius=1.55
    g8: Circle CenterX=-13.5 CenterY=96 CenterZ=0 NormalX=0 NormalY=0 NormalZ=1 AngleXU=0 Radius=1.55
    g9: Circle CenterX=13.5 CenterY=96 CenterZ=0 NormalX=0 NormalY=0 NormalZ=1 AngleXU=0 Radius=1.55
    g10: Circle CenterX=-13.5 CenterY=40 CenterZ=0 NormalX=0 NormalY=0 NormalZ=1 AngleXU=0 Radius=1.55
    g11: Circle CenterX=13.5 CenterY=40 CenterZ=0 NormalX=0 NormalY=0 NormalZ=1 AngleXU=0 Radius=1.55
  constraints (30):
    c: Coincident(g0,g1)
    c: Coincident(g1,g2)
    c: Coincident(g2,g3)
    c: Coincident(g3,g0)
    c: Horizontal(g0)
    c: Vertical(g1)
    c: Vertical(g3)
    c: DistanceX(g2,g2) = 35
    c: Equal(g7,g6)
    c: Equal(g6,g4)
    c: Equal(g4,g5)
    c: Symmetric(g6,g7,g-2)
    c: Symmetric(g4,g6,g-1)
    c: Symmetric(g5,g7,g-1)
    c: Diameter(g7) = 3.1
    c: DistanceX(g6,g7) = 30.5
    c: DistanceY(g7,g5) = 30.5
    c: Symmetric(g2,g1,g-2)
    c: DistanceY(g1,g-1) = 20
    c: DistanceY(g3,g3) = 120
    c: Symmetric(g8,g9,g-2)
    c: Diameter(g9) = 3.1
    c: Equal(g9,g8)
    c: DistanceX(g9,g0) = 4
    c: DistanceY(g9,g0) = 4
    c: Equal(g11,g10)
    c: Symmetric(g10,g11,g-2)
    c: Diameter(g11) = 3.1
    c: DistanceX(g11,g0) = 4
    c: DistanceY(g11,g0) = 60
FEATURE [PartDesign::Pad] Pad
  Direction = (0,0,1)
  Length = 2
  Length2 = 10
  Profile = -> Sketch
  ReferenceAxis = -> Sketch [N_Axis]
  Type = 0
FEATURE [PartDesign::CoordinateSystem] LCS_1
  AttacherType = Attacher::AttachEngine3D
  MapMode = 11
  Placement = pos=(15.25,15.25,0) rot=(0,0,1;1.5708rad)
  Support = -> [Pad]
FEATURE [PartDesign::CoordinateSystem] LCS_2
  AttacherType = Attacher::AttachEngine3D
  MapMode = 11
  Placement = pos=(-13.5,96,2) rot=(0,0,1;1.5708rad)
  Support = -> [Pad]
FEATURE [PartDesign::CoordinateSystem] LCS_3
  AttacherType = Attacher::AttachEngine3D
  MapMode = 11
  Placement = pos=(13.5,96,2) rot=(0,0,1;1.5708rad)
  Support = -> [Pad]
FEATURE [PartDesign::CoordinateSystem] LCS_4
  AttacherType = Attacher::AttachEngine3D
  MapMode = 11
  Placement = pos=(-13.5,40,2) rot=(0,0,1;1.5708rad)
  Support = -> [Pad]
FEATURE [PartDesign::CoordinateSystem] LCS_5
  AttacherType = Attacher::AttachEngine3D
  MapMode = 11
  Placement = pos=(13.5,40,2) rot=(0,0,1;1.5708rad)
  Support = -> [Pad]
FEATURE [PartDesign::Body] Body
  Group = -> [Sketch,Pad,LCS_1,LCS_2,LCS_3,LCS_4,LCS_5]
  Origin = -> Origin
  Tip = -> Pad
---- part motor_1810.FCStd = doc fcstd_5295c51692c7 ----
FCSTD DOCUMENT  (FreeCAD 0.20R29410 (Git))
Label: motor_1810
License: All rights reserved
LicenseURL: http://en.wikipedia.org/wiki/All_rights_reserved
objects: Sketcher::SketchObject×9, PartDesign::Pad×7, PartDesign::Pocket×2, PartDesign::CoordinateSystem×2, PartDesign::Body×1
note: 30 computed .brp shape members not serialized (recipe doc carries the construction recipe); baked Part::Feature solids carry a one-line shape summary decoded from their .brp

FEATURE [Sketcher::SketchObject] Sketch
  FullyConstrained = true
  MapMode = 5
  Support = -> [XY_Plane]
  sketch-geometry (16):
    g0: LineSegment StartX=4.75 StartY=-2.74241 StartZ=0 EndX=9e-16 EndY=5.48483 EndZ=0
    g1: LineSegment StartX=1.1e-15 StartY=5.48483 StartZ=0 EndX=-4.75 EndY=-2.74241 EndZ=0
    g2: LineSegment StartX=-4.75 StartY=-2.74241 StartZ=0 EndX=4.75 EndY=-2.74241 EndZ=0
    g3: Circle CenterX=0 CenterY=0 CenterZ=0 NormalX=0 NormalY=0 NormalZ=1 AngleXU=0 Radius=5.48483
    g4: ArcOfCircle CenterX=4.75 CenterY=-2.74241 CenterZ=0 NormalX=0 NormalY=0 NormalZ=1 AngleXU=0 Radius=2 StartAngle=4.00544 EndAngle=7.51373
    g5: ArcOfCircle CenterX=1.1e-15 CenterY=5.48483 CenterZ=0 NormalX=0 NormalY=0 NormalZ=1 AngleXU=0 Radius=2 StartAngle=6.09984 EndAngle=9.60812
    g6: ArcOfCircle CenterX=-4.75 CenterY=-2.74241 CenterZ=0 NormalX=0 NormalY=0 NormalZ=1 AngleXU=0 Radius=2 StartAngle=1.91105 EndAngle=5.41933
    g7: LineSegment StartX=1.96648 StartY=5.12019 StartZ=0 EndX=1.96648 EndY=3.19303 EndZ=0
    g8: LineSegment StartX=-1.96648 StartY=5.12019 StartZ=0 EndX=-1.96648 EndY=3.19303 EndZ=0
    g9: LineSegment StartX=-5.41745 StartY=-0.857073 StartZ=0 EndX=-3.74849 EndY=0.106503 EndZ=0
    g10: LineSegment StartX=-3.45097 StartY=-4.26311 StartZ=0 EndX=-1.78201 EndY=-3.29954 EndZ=0
    g11: LineSegment StartX=3.45097 StartY=-4.26311 StartZ=0 EndX=1.78201 EndY=-3.29954 EndZ=0
    g12: LineSegment StartX=5.41745 StartY=-0.857073 StartZ=0 EndX=3.74849 EndY=0.106503 EndZ=0
    g13: ArcOfCircle CenterX=0 CenterY=0 CenterZ=0 NormalX=0 NormalY=0 NormalZ=1 AngleXU=0 Radius=3.75 StartAngle=2.1228 EndAngle=3.11319
    g14: ArcOfCircle CenterX=0 CenterY=0 CenterZ=0 NormalX=0 NormalY=0 NormalZ=1 AngleXU=0 Radius=3.75 StartAngle=0.0284047 EndAngle=1.01879
    g15: ArcOfCircle CenterX=0 CenterY=0 CenterZ=0 NormalX=0 NormalY=0 NormalZ=1 AngleXU=0 Radius=3.75 StartAngle=4.21719 EndAngle=5.20758
  constraints (47):
    c: Coincident(g0,g1)
    c: Coincident(g1,g2)
    c: Coincident(g2,g0)
    c: Equal(g0,g1)
    c: Equal(g0,g2)
    c: PointOnObject(g0,g3)
    c: PointOnObject(g1,g3)
    c: PointOnObject(g2,g3)
    c: Horizontal(g2)
    c: Coincident(g3,g-1)
    c: DistanceX(g1,g0) = 9.5
    c: Coincident(g4,g0)
    c: PointOnObject(g4,g3)
    c: PointOnObject(g4,g3)
    c: Coincident(g5,g0)
    c: PointOnObject(g5,g3)
    c: PointOnObject(g5,g3)
    c: Coincident(g6,g1)
    c: PointOnObject(g6,g3)
    c: PointOnObject(g6,g3)
    c: Equal(g6,g5)
    c: Equal(g5,g4)
    c: Diameter(g5) = 4
    c: Coincident(g7,g5)
    c: Vertical(g7)
    c: Coincident(g8,g5)
    c: Vertical(g8)
    c: Coincident(g9,g6)
    c: Coincident(g10,g6)
    c: Coincident(g11,g4)
    c: Coincident(g12,g4)
    c: Coincident(g13,g3)
    c: Coincident(g13,g9)
    c: Coincident(g13,g8)
    c: Coincident(g14,g13)
    c: Coincident(g14,g7)
    c: Coincident(g14,g12)
    c: Coincident(g15,g13)
    c: Coincident(g15,g10)
    c: Coincident(g15,g11)
    c: Equal(g11,g12)
    c: Equal(g12,g7)
    c: Equal(g7,g8)
    c: Equal(g8,g9)
    c: Equal(g9,g10)
    c: Angle(g10) = 0.523599
    c: Diameter(g14) = 7.5
FEATURE [PartDesign::Pad] Pad
  Direction = (0,0,1)
  Length = 3
  Length2 = 10
  Profile = -> Sketch
  ReferenceAxis = -> Sketch [N_Axis]
  Type = 0
FEATURE [Sketcher::SketchObject] Sketch001
  FullyConstrained = true
  MapMode = 5
  Placement = pos=(0,0,3) rot=(0,0,1;0rad)
  Support = -> [Pad]
  sketch-geometry (1):
    g0: Circle CenterX=0 CenterY=0 CenterZ=0 NormalX=0 NormalY=0 NormalZ=1 AngleXU=0 Radius=9
  constraints (2):
    c: Coincident(g0,g-1)
    c: Diameter(g0) = 18
FEATURE [PartDesign::Pad] Pad001
  BaseFeature = -> Pad
  Direction = (0,0,1)
  Length = 10
  Length2 = 10
  Profile = -> Sketch001
  ReferenceAxis = -> Sketch001 [N_Axis]
  Type = 0
FEATURE [Sketcher::SketchObject] Sketch002
  FullyConstrained = true
  MapMode = 5
  Placement = pos=(0,0,13) rot=(0,0,1;0rad)
  Support = -> [Pad001]
  sketch-geometry (1):
    g0: Circle CenterX=0 CenterY=0 CenterZ=0 NormalX=0 NormalY=0 NormalZ=1 AngleXU=0 Radius=8.2
  constraints (2):
    c: Coincident(g0,g-1)
    c: Diameter(g0) = 16.4
FEATURE [PartDesign::Pad] Pad002
  BaseFeature = -> Pad001
  Direction = (0,0,1)
  Length = 1.3
  Length2 = 10
  Profile = -> Sketch002
  ReferenceAxis = -> Sketch002 [N_Axis]
  Type = 0
FEATURE [Sketcher::SketchObject] Sketch003
  FullyConstrained = true
  MapMode = 5
  Placement = pos=(0,0,14.3) rot=(0,0,1;0rad)
  Support = -> [Pad002]
  sketch-geometry (1):
    g0: Circle CenterX=0 CenterY=0 CenterZ=0 NormalX=0 NormalY=0 NormalZ=1 AngleXU=0 Radius=1
  constraints (2):
    c: Coincident(g0,g-1)
    c: Diameter(g0) = 2
FEATURE [PartDesign::Pad] Pad003
  BaseFeature = -> Pad002
  Direction = (0,0,1)
  Length = 2.5
  Length2 = 10
  Profile = -> Sketch003
  ReferenceAxis = -> Sketch003 [N_Axis]
  Type = 0
FEATURE [Sketcher::SketchObject] Sketch004
  ExternalGeometry = -> [Pad003]
  FullyConstrained = true
  MapMode = 5
  Placement = pos=(0,0,0) rot=(1,0,0;3.14159rad)
  Support = -> [Pad003]
  sketch-geometry (3):
    g0: Circle CenterX=4.75 CenterY=2.74241 CenterZ=0 NormalX=0 NormalY=0 NormalZ=1 AngleXU=0 Radius=1
    g1: Circle CenterX=-4.75 CenterY=2.74241 CenterZ=0 NormalX=0 NormalY=0 NormalZ=1 AngleXU=0 Radius=1
    g2: Circle CenterX=0 CenterY=-5.48483 CenterZ=0 NormalX=0 NormalY=0 NormalZ=1 AngleXU=0 Radius=1
  constraints (6):
    c: Coincident(g0,g-3)
    c: Coincident(g1,g-4)
    c: Coincident(g2,g-5)
    c: Equal(g0,g1)
    c: Equal(g1,g2)
    c: Diameter(g0) = 2
FEATURE [PartDesign::Pocket] Pocket
  BaseFeature = -> Pad003
  Direction = (0,0,1)
  Length = 3
  Length2 = 5
  Profile = -> Sketch004
  ReferenceAxis = -> Sketch004 [N_Axis]
  Type = 0
FEATURE [Sketcher::SketchObject] Sketch005
  FullyConstrained = true
  MapMode = 5
  Placement = pos=(0,0,14.3) rot=(0,0,1;0rad)
  Support = -> [Pocket]
  sketch-geometry (10):
    g0: Circle CenterX=0 CenterY=5.5 CenterZ=0 NormalX=0 NormalY=0 NormalZ=1 AngleXU=0 Radius=1
    g1: Circle CenterX=0 CenterY=-5.5 CenterZ=0 NormalX=0 NormalY=0 NormalZ=1 AngleXU=0 Radius=1
    g2: ArcOfCircle CenterX=0 CenterY=0 CenterZ=0 NormalX=0 NormalY=0 NormalZ=1 AngleXU=0 Radius=3 StartAngle=2.35619 EndAngle=3.92699
    g3: ArcOfCircle CenterX=0 CenterY=0 CenterZ=0 NormalX=0 NormalY=0 NormalZ=1 AngleXU=0 Radius=7 StartAngle=2.35619 EndAngle=3.92699
    g4: ArcOfCircle CenterX=0 CenterY=0 CenterZ=0 NormalX=0 NormalY=0 NormalZ=1 AngleXU=0 Radius=3 StartAngle=5.49779 EndAngle=7.06858
    g5: ArcOfCircle CenterX=0 CenterY=0 CenterZ=0 NormalX=0 NormalY=0 NormalZ=1 AngleXU=0 Radius=7 StartAngle=5.49779 EndAngle=7.06858
    g6: ArcOfCircle CenterX=-3.53553 CenterY=3.53553 CenterZ=0 NormalX=0 NormalY=0 NormalZ=1 AngleXU=0 Radius=2 StartAngle=5.49779 EndAngle=8.63938
    g7: ArcOfCircle CenterX=3.53553 CenterY=3.53553 CenterZ=0 NormalX=0 NormalY=0 NormalZ=1 AngleXU=0 Radius=2 StartAngle=0.785398 EndAngle=3.92699
    g8: ArcOfCircle CenterX=3.53553 CenterY=-3.53553 CenterZ=0 NormalX=0 NormalY=0 NormalZ=1 AngleXU=0 Radius=2 StartAngle=2.35619 EndAngle=5.49779
    g9: ArcOfCircle CenterX=-3.53553 CenterY=-3.53553 CenterZ=0 NormalX=0 NormalY=0 NormalZ=1 AngleXU=0 Radius=2 StartAngle=3.92698 EndAngle=7.06858
  constraints (29):
    c: PointOnObject(g0,g-2)
    c: Symmetric(g1,g0,g-1)
    c: Equal(g1,g0)
    c: Diameter(g1) = 2
    c: DistanceY(g1,g0) = 11
    c: Coincident(g2,g-1)
    c: Coincident(g3,g2)
    c: Coincident(g4,g2)
    c: Coincident(g5,g2)
    c: Symmetric(g2,g4,g-2)
    c: Vertical(g2,g2)
    c: Vertical(g4,g4)
    c: Diameter(g4) = 6
    c: Symmetric(g3,g5,g-2)
    c: Diameter(g5) = 14
    c: Coincident(g6,g3)
    c: Coincident(g6,g2)
    c: Coincident(g7,g4)
    c: Coincident(g7,g5)
    c: Coincident(g8,g4)
    c: Coincident(g8,g5)
    c: Coincident(g9,g2)
    c: Coincident(g9,g3)
    c: Symmetric(g9,g8,g-2)
    c: Symmetric(g8,g7,g-1)
    c: Angle(g4) = 1.5708
    c: Angle(g5) = 1.5708
    c: Angle(g8) = 3.14159
    c: Angle(g6) = 3.14159
FEATURE [PartDesign::Pocket] Pocket001
  BaseFeature = -> Pocket
  Direction = (0,0,-1)
  Length = 3
  Length2 = 5
  Profile = -> Sketch005
  ReferenceAxis = -> Sketch005 [N_Axis]
  Type = 0
FEATURE [Sketcher::SketchObject] Sketch006
  FullyConstrained = true
  MapMode = 5
  Placement = pos=(0,0,0) rot=(1,0,0;3.14159rad)
  Support = -> [Pocket001]
  sketch-geometry (1):
    g0: Circle CenterX=0 CenterY=0 CenterZ=0 NormalX=0 NormalY=0 NormalZ=1 AngleXU=0 Radius=2
  constraints (2):
    c: Coincident(g0,g-1)
    c: Diameter(g0) = 4
FEATURE [PartDesign::Pad] Pad004
  BaseFeature = -> Pocket001
  Direction = (0,0,-1)
  Length = 0.6
  Length2 = 10
  Profile = -> Sketch006
  ReferenceAxis = -> Sketch006 [N_Axis]
  Type = 0
FEATURE [Sketcher::SketchObject] Sketch007
  FullyConstrained = true
  MapMode = 5
  Placement = pos=(0,0,-0.6) rot=(1,0,0;3.14159rad)
  Support = -> [Pad004]
  sketch-geometry (1):
    g0: Circle CenterX=0 CenterY=0 CenterZ=0 NormalX=0 NormalY=0 NormalZ=1 AngleXU=0 Radius=1
  constraints (2):
    c: Coincident(g0,g-1)
    c: Diameter(g0) = 2
FEATURE [PartDesign::Pad] Pad005
  BaseFeature = -> Pad004
  Direction = (0,0,-1)
  Length = 1
  Length2 = 10
  Profile = -> Sketch007
  ReferenceAxis = -> Sketch007 [N_Axis]
  Type = 0
FEATURE [Sketcher::SketchObject] Sketch008
  ExternalGeometry = -> [Pad005]
  FullyConstrained = true
  MapMode = 5
  Placement = pos=(0,0,3) rot=(1,0,0;3.14159rad)
  Support = -> [Pad005]
  sketch-geometry (4):
    g0: LineSegment StartX=-2.5 StartY=5.75 StartZ=0 EndX=2.5 EndY=5.75 EndZ=0
    g1: LineSegment StartX=2.5 StartY=5.75 StartZ=0 EndX=2.5 EndY=3.75 EndZ=0
    g2: LineSegment StartX=2.5 StartY=3.75 StartZ=0 EndX=-2.5 EndY=3.75 EndZ=0
    g3: LineSegment StartX=-2.5 StartY=3.75 StartZ=0 EndX=-2.5 EndY=5.75 EndZ=0
  constraints (11):
    c: Coincident(g0,g1)
    c: Coincident(g1,g2)
    c: Coincident(g2,g3)
    c: Coincident(g3,g0)
    c: Horizontal(g2)
    c: Vertical(g1)
    c: Vertical(g3)
    c: DistanceY(g1,g1) = 2
    c: DistanceX(g0,g0) = 5
    c: Tangent(g2,g-3)
    c: Symmetric(g0,g0,g-2)
FEATURE [PartDesign::Pad] Pad006
  BaseFeature = -> Pad005
  Direction = (0,0,-1)
  Length = 8
  Length2 = 10
  Profile = -> Sketch008
  ReferenceAxis = -> Sketch008 [N_Axis]
  Type = 0
FEATURE [PartDesign::CoordinateSystem] LCS_1
  AttacherType = Attacher::AttachEngine3D
  MapMode = 11
  Placement = pos=(0,0,0) rot=(0.707107,-0.707107,0;3.14159rad)
  Support = -> [Pad006]
FEATURE [PartDesign::CoordinateSystem] LCS_2
  AttacherType = Attacher::AttachEngine3D
  MapMode = 11
  Placement = pos=(0,0,14.3) rot=(0,0,1;1.5708rad)
  Support = -> [Pad006]
FEATURE [PartDesign::Body] Body
  Group = -> [Sketch,Pad,Sketch001,Pad001,Sketch002,Pad002,Sketch003,Pad003,Sketch004,Pocket,Sketch005,Pocket001,Sketch006,Pad004,Sketch007,Pad005,Sketch008,Pad006,LCS_1,LCS_2]
  Origin = -> Origin
  Tip = -> Pad006
---- part prop.FCStd = doc fcstd_233e3b54224a ----
FCSTD DOCUMENT  (FreeCAD 0.20R29410 (Git))
Label: prop
License: All rights reserved
LicenseURL: http://en.wikipedia.org/wiki/All_rights_reserved
objects: Sketcher::SketchObject×12, Part::Fuse×4, Part::Loft×3, PartDesign::Pad×2, Part::FeaturePython×1, PartDesign::FeatureBase×1, PartDesign::Point×1, PartDesign::Plane×1, PartDesign::AdditiveLoft×1, PartDesign::Pocket×1, PartDesign::CoordinateSystem×1, PartDesign::Body×1
note: 33 computed .brp shape members not serialized (recipe doc carries the construction recipe); baked Part::Feature solids carry a one-line shape summary decoded from their .brp

FEATURE [Sketcher::SketchObject] Sketch
  FullyConstrained = true
  MapMode = 5
  Support = -> [XY_Plane]
  sketch-geometry (38):
    g0: LineSegment StartX=0 StartY=-3 StartZ=0 EndX=0 EndY=3 EndZ=0
    g1: LineSegment StartX=0 StartY=3 StartZ=0 EndX=9 EndY=3 EndZ=0
    g2: LineSegment StartX=0 StartY=-3 StartZ=0 EndX=9 EndY=-3 EndZ=0
    g3: LineSegment StartX=9 StartY=3 StartZ=0 EndX=19 EndY=7 EndZ=0
    g4: LineSegment StartX=19 StartY=7 StartZ=0 EndX=69 EndY=3 EndZ=0
    g5: LineSegment StartX=69 StartY=3 StartZ=0 EndX=69 EndY=-5 EndZ=0
    g6: LineSegment StartX=9 StartY=-3 StartZ=0 EndX=13 EndY=-5 EndZ=0
    g7: LineSegment StartX=13 StartY=-5 StartZ=0 EndX=18 EndY=-12 EndZ=0
    g8: LineSegment StartX=18 StartY=-12 StartZ=0 EndX=69 EndY=-5 EndZ=0
    g9: GeomPoint X=5 Y=0 Z=0
    g10: GeomPoint X=10 Y=0 Z=0
    g11: GeomPoint X=15 Y=0 Z=0
    g12: GeomPoint X=20 Y=0 Z=0
    g13: GeomPoint X=25 Y=0 Z=0
    g14: GeomPoint X=30 Y=0 Z=0
    g15: GeomPoint X=35 Y=0 Z=0
    g16: GeomPoint X=40 Y=0 Z=0
    g17: GeomPoint X=45 Y=0 Z=0
    g18: GeomPoint X=50 Y=0 Z=0
    g19: GeomPoint X=55 Y=0 Z=0
    g20: GeomPoint X=60 Y=0 Z=0
    g21: GeomPoint X=65 Y=0 Z=0
    g22: GeomPoint X=69 Y=0 Z=0
    g23: LineSegment StartX=0 StartY=16.18 StartZ=0 EndX=32.3915 EndY=-10.0247 EndZ=0
    g24: ArcOfCircle CenterX=20 CenterY=0 CenterZ=0 NormalX=0 NormalY=0 NormalZ=1 AngleXU=0 Radius=6.92 StartAngle=1.5708 EndAngle=3.14159
    g25: LineSegment StartX=13.08 StartY=8e-16 StartZ=0 EndX=13.08 EndY=5.59828 EndZ=0
    g26: ArcOfCircle CenterX=20 CenterY=0 CenterZ=0 NormalX=0 NormalY=0 NormalZ=1 AngleXU=0 Radius=11.7255 StartAngle=4.71239 EndAngle=6.28319
    g27: LineSegment StartX=31.7255 StartY=-2.9e-15 StartZ=0 EndX=31.7255 EndY=-9.48592 EndZ=0
    g28: LineSegment StartX=0 StartY=16.18 StartZ=0 EndX=87.6232 EndY=-4.367 EndZ=0
    g29: ArcOfCircle CenterX=69 CenterY=0 CenterZ=0 NormalX=0 NormalY=0 NormalZ=1 AngleXU=0 Radius=3 StartAngle=1.5708 EndAngle=3.14159
    g30: ArcOfCircle CenterX=69 CenterY=0 CenterZ=0 NormalX=0 NormalY=0 NormalZ=1 AngleXU=0 Radius=5 StartAngle=4.71239 EndAngle=6.28319
    g31: LineSegment StartX=66 StartY=4e-16 StartZ=0 EndX=66 EndY=0.703478 EndZ=0
    g32: LineSegment StartX=74 StartY=-1.2e-15 StartZ=0 EndX=74 EndY=-1.17246 EndZ=0
    g33: LineSegment StartX=0 StartY=16.18 StartZ=0 EndX=22.3034 EndY=-11.4093 EndZ=0
    g34: ArcOfCircle CenterX=13.08 CenterY=8e-16 CenterZ=0 NormalX=0 NormalY=0 NormalZ=1 AngleXU=0 Radius=4.632 StartAngle=1.5708 EndAngle=3.14159
    g35: ArcOfCircle CenterX=13.08 CenterY=8e-16 CenterZ=0 NormalX=0 NormalY=0 NormalZ=1 AngleXU=0 Radius=5.00064 StartAngle=4.69639 EndAngle=6.28319
    g36: LineSegment StartX=8.448 StartY=1.4e-15 StartZ=0 EndX=8.448 EndY=5.7298 EndZ=0
    g37: LineSegment StartX=18.0806 StartY=-4e-16 StartZ=0 EndX=18.0806 EndY=-6.18581 EndZ=0
  constraints (103):
    c: PointOnObject(g0,g-2)
    c: DistanceY(g0,g0) = 6
    c: Symmetric(g0,g0,g-1)
    c: Coincident(g1,g0)
    c: Horizontal(g1)
    c: Coincident(g2,g0)
    c: Horizontal(g2)
    c: Equal(g2,g1)
    c: DistanceX(g1,g1) = 9
    c: Coincident(g3,g1)
    c: DistanceX(g1,g3) = 10
    c: DistanceY(g1,g3) = 4
    c: Coincident(g4,g3)
    c: DistanceX(g3,g4) = 50
    c: DistanceY(g4,g3) = 4
    c: Coincident(g5,g4)
    c: Vertical(g5)
    c: DistanceY(g5,g5) = 8
    c: Coincident(g6,g2)
    c: DistanceY(g6,g2) = 2
    c: DistanceX(g2,g6) = 4
    c: Coincident(g7,g6)
    c: DistanceX(g6,g7) = 5
    c: DistanceY(g7,g6) = 7
    c: Coincident(g8,g7)
    c: Coincident(g8,g5)
    c: PointOnObject(g9,g-1)
    c: DistanceX(g-1,g9) = 5
    c: PointOnObject(g10,g-1)
    c: PointOnObject(g11,g-1)
    c: PointOnObject(g12,g-1)
    c: PointOnObject(g13,g-1)
    c: DistanceX(g10) = 10
    c: DistanceX(g11) = 15
    c: DistanceX(g12) = 20
    c: DistanceX(g13) = 25
    c: PointOnObject(g14,g-1)
    c: PointOnObject(g15,g-1)
    c: PointOnObject(g16,g-1)
    c: PointOnObject(g17,g-1)
    c: PointOnObject(g18,g-1)
    c: PointOnObject(g19,g-1)
    c: DistanceX(g14) = 30
    c: DistanceX(g15) = 35
    c: DistanceX(g16) = 40
    c: DistanceX(g17) = 45
    c: DistanceX(g18) = 50
    c: DistanceX(g19) = 55
    c: PointOnObject(g20,g-1)
    c: PointOnObject(g21,g-1)
    c: PointOnObject(g22,g5)
    c: PointOnObject(g22,g-1)
    c: DistanceX(g20) = 60
    c: DistanceX(g21) = 65
    c: PointOnObject(g23,g-2)
    c: DistanceY(g23) = 16.18
    c: PointOnObject(g12,g23)
    c: Coincident(g24,g12)
    c: PointOnObject(g24,g4)
    c: PointOnObject(g24,g-1)
    c: Coincident(g25,g24)
    c: PointOnObject(g25,g23)
    c: Vertical(g25)
    c: Vertical(g24,g12)
    c: PointOnObject(g23,g8)
    c: Coincident(g26,g12)
    c: PointOnObject(g26,g8)
    c: PointOnObject(g26,g-1)
    c: Vertical(g26,g12)
    c: Coincident(g27,g26)
    c: Vertical(g27)
    c: PointOnObject(g27,g23)
    c: Coincident(g28,g23)
    c: PointOnObject(g22,g28)
    c: Distance(g28) = 90
    c: Coincident(g29,g22)
    c: Coincident(g29,g4)
    c: PointOnObject(g29,g-1)
    c: Coincident(g30,g22)
    c: Coincident(g30,g5)
    c: PointOnObject(g30,g-1)
    c: Coincident(g31,g29)
    c: PointOnObject(g31,g28)
    c: Vertical(g31)
    c: Coincident(g32,g30)
    c: PointOnObject(g32,g28)
    c: Vertical(g32)
    c: Coincident(g33,g23)
    c: PointOnObject(g33,g8)
    c: PointOnObject(g24,g33)
    c: Coincident(g34,g24)
    c: PointOnObject(g34,g3)
    c: PointOnObject(g34,g-1)
    c: Coincident(g35,g24)
    c: Coincident(g35,g6)
    c: PointOnObject(g35,g-1)
    c: Vertical(g34,g24)
    c: Coincident(g36,g34)
    c: PointOnObject(g36,g33)
    c: Vertical(g36)
    c: Coincident(g37,g35)
    c: PointOnObject(g37,g33)
    c: Vertical(g37)
FEATURE [Sketcher::SketchObject] Sketch001
  FullyConstrained = true
  Placement = pos=(20,0,0) rot=(0.57735,0.57735,0.57735;2.0944rad)
  sketch-geometry (8):
    g0: LineSegment StartX=-11.7243 StartY=-9.48401 StartZ=0 EndX=6.91953 EndY=5.59733 EndZ=0
    g1: LineSegment StartX=0 StartY=0 StartZ=0 EndX=-1.88674 EndY=2.33243 EndZ=0
    g2: Circle CenterX=-11.7243 CenterY=-9.48401 CenterZ=0 NormalX=0 NormalY=0 NormalZ=1 AngleXU=0 Radius=1
    g3: Circle CenterX=-1.88674 CenterY=2.33243 CenterZ=0 NormalX=0 NormalY=0 NormalZ=1 AngleXU=0 Radius=1
    g4: Circle CenterX=6.91953 CenterY=5.59733 CenterZ=0 NormalX=0 NormalY=0 NormalZ=1 AngleXU=0 Radius=1
    g5: BSplineCurve PolesCount=3 KnotsCount=2 Degree=2 IsPeriodic=0
    g6: GeomPoint X=-11.7243 Y=-9.48401 Z=0
    g7: GeomPoint X=6.91953 Y=5.59733 Z=0
  constraints (18):
    c: PointOnObject(g-1,g0)
    c: Distance(g-1,g0) = 8.9
    c: Distance(g-1,g0) = 15.08
    c: Angle(g0,g-1) = 2.46144
    c: Coincident(g1,g-1)
    c: Distance(g1) = 3
    c: Angle(g1,g0) = 1.5708
    c: Weight(g2) = 1
    c: Coincident(g5,g0)
    c: Equal(g2,g3)
    c: Coincident(g3,g1)
    c: Equal(g2,g4)
    c: Coincident(g5,g0)
    c: InternalAlignment(g2,g5)
    c: InternalAlignment(g3,g5)
    c: InternalAlignment(g4,g5)
    c: InternalAlignment(g6,g5)
    c: InternalAlignment(g7,g5)
FEATURE [Sketcher::SketchObject] Sketch002
  FullyConstrained = true
  Placement = pos=(50,0,0) rot=(0.57735,0.57735,0.57735;2.0944rad)
  sketch-geometry (8):
    g0: LineSegment StartX=-7.60195 StartY=-2.45976 StartZ=0 EndX=4.51931 EndY=1.46231 EndZ=0
    g1: LineSegment StartX=0 StartY=0 StartZ=0 EndX=-0.923564 EndY=2.8543 EndZ=0
    g2: Circle CenterX=4.51931 CenterY=1.46231 CenterZ=0 NormalX=0 NormalY=0 NormalZ=1 AngleXU=0 Radius=1
    g3: Circle CenterX=-0.923564 CenterY=2.8543 CenterZ=0 NormalX=0 NormalY=0 NormalZ=1 AngleXU=0 Radius=1
    g4: Circle CenterX=-7.60195 CenterY=-2.45976 CenterZ=0 NormalX=0 NormalY=0 NormalZ=1 AngleXU=0 Radius=1
    g5: BSplineCurve PolesCount=3 KnotsCount=2 Degree=2 IsPeriodic=0
    g6: GeomPoint X=4.51931 Y=1.46231 Z=0
    g7: GeomPoint X=-7.60195 Y=-2.45976 Z=0
  constraints (18):
    c: PointOnObject(g-1,g0)
    c: Distance(g-1,g0) = 4.75
    c: Distance(g-1,g0) = 7.99
    c: Angle(g0,g-1) = 2.82866
    c: Coincident(g1,g-1)
    c: Angle(g1,g0) = 1.5708
    c: Distance(g1) = 3
    c: Weight(g2) = 1
    c: Coincident(g5,g0)
    c: Equal(g2,g3)
    c: Coincident(g3,g1)
    c: Equal(g2,g4)
    c: Coincident(g5,g0)
    c: InternalAlignment(g2,g5)
    c: InternalAlignment(g3,g5)
    c: InternalAlignment(g4,g5)
    c: InternalAlignment(g6,g5)
    c: InternalAlignment(g7,g5)
FEATURE [Sketcher::SketchObject] Sketch003
  FullyConstrained = true
  Placement = pos=(69,0,0) rot=(0.57735,0.57735,0.57735;2.0944rad)
  sketch-geometry (8):
    g0: LineSegment StartX=-4.99466 StartY=-1.17057 StartZ=0 EndX=2.99875 EndY=0.702797 EndZ=0
    g1: LineSegment StartX=0 StartY=0 StartZ=0 EndX=-0.684543 EndY=2.92086 EndZ=0
    g2: Circle CenterX=2.99875 CenterY=0.702797 CenterZ=0 NormalX=0 NormalY=0 NormalZ=1 AngleXU=0 Radius=1
    g3: Circle CenterX=-0.684543 CenterY=2.92086 CenterZ=0 NormalX=0 NormalY=0 NormalZ=1 AngleXU=0 Radius=1
    g4: Circle CenterX=-4.99466 CenterY=-1.17057 CenterZ=0 NormalX=0 NormalY=0 NormalZ=1 AngleXU=0 Radius=1
    g5: BSplineCurve PolesCount=3 KnotsCount=2 Degree=2 IsPeriodic=0
    g6: GeomPoint X=2.99875 Y=0.702797 Z=0
    g7: GeomPoint X=-4.99466 Y=-1.17057 Z=0
  constraints (18):
    c: PointOnObject(g-1,g0)
    c: Angle(g0,g-1) = 2.91138
    c: Coincident(g1,g-1)
    c: Angle(g1,g0) = 1.5708
    c: Distance(g1) = 3
    c: Distance(g1,g0) = 3.08
    c: Distance(g1,g0) = 5.13
    c: Weight(g2) = 1
    c: Coincident(g5,g0)
    c: Equal(g2,g3)
    c: Coincident(g3,g1)
    c: Equal(g2,g4)
    c: Coincident(g5,g0)
    c: InternalAlignment(g2,g5)
    c: InternalAlignment(g3,g5)
    c: InternalAlignment(g4,g5)
    c: InternalAlignment(g6,g5)
    c: InternalAlignment(g7,g5)
FEATURE [Sketcher::SketchObject] Sketch004
  FullyConstrained = true
  Placement = pos=(0,0,0) rot=(0.57735,0.57735,0.57735;2.0944rad)
  sketch-geometry (4):
    g0: ArcOfCircle CenterX=-1 CenterY=0 CenterZ=0 NormalX=0 NormalY=0 NormalZ=1 AngleXU=0 Radius=2 StartAngle=1.5708 EndAngle=4.71239
    g1: ArcOfCircle CenterX=1 CenterY=0 CenterZ=0 NormalX=0 NormalY=0 NormalZ=1 AngleXU=0 Radius=2 StartAngle=4.71239 EndAngle=7.85398
    g2: LineSegment StartX=-1 StartY=-2 StartZ=0 EndX=1 EndY=-2 EndZ=0
    g3: LineSegment StartX=1 StartY=2 StartZ=0 EndX=-1 EndY=2 EndZ=0
  constraints (9):
    c: Tangent(g0,g2) = -1.5708
    c: Tangent(g2,g1) = -1.5708
    c: Tangent(g1,g3) = -1.5708
    c: Tangent(g3,g0) = -1.5708
    c: Equal(g0,g1)
    c: PointOnObject(g0,g-1)
    c: Symmetric(g0,g1,g-2)
    c: DistanceY(g1,g1) = 4
    c: DistanceX(g0,g1) = 2
FEATURE [Sketcher::SketchObject] Sketch005
  FullyConstrained = true
  Placement = pos=(9,0,0) rot=(0.57735,0.57735,0.57735;2.0944rad)
  sketch-geometry (7):
    g0: Circle CenterX=3 CenterY=0 CenterZ=0 NormalX=0 NormalY=0 NormalZ=1 AngleXU=0 Radius=1
    g1: Circle CenterX=0 CenterY=2 CenterZ=0 NormalX=0 NormalY=0 NormalZ=1 AngleXU=0 Radius=1
    g2: Circle CenterX=-3 CenterY=4e-16 CenterZ=0 NormalX=0 NormalY=0 NormalZ=1 AngleXU=0 Radius=1
    g3: BSplineCurve PolesCount=3 KnotsCount=2 Degree=2 IsPeriodic=0
    g4: GeomPoint X=3 Y=0 Z=0
    g5: GeomPoint X=-3 Y=4e-16 Z=0
    g6: ArcOfCircle CenterX=0 CenterY=4 CenterZ=0 NormalX=0 NormalY=0 NormalZ=1 AngleXU=0 Radius=5 StartAngle=4.06889 EndAngle=5.35589
  constraints (17):
    c: Weight(g0) = 1
    c: PointOnObject(g3,g-1)
    c: Equal(g0,g1)
    c: PointOnObject(g1,g-2)
    c: Equal(g0,g2)
    c: InternalAlignment(g0,g3)
    c: InternalAlignment(g1,g3)
    c: InternalAlignment(g2,g3)
    c: InternalAlignment(g4,g3)
    c: InternalAlignment(g5,g3)
    c: DistanceY(g-1,g1) = 2
    c: PointOnObject(g6,g-2)
    c: Coincident(g6,g3)
    c: Coincident(g6,g3)
    c: PointOnObject(g3,g-1)
    c: DistanceX(g3,g3) = 6
    c: Diameter(g6) = 10
FEATURE [Sketcher::SketchObject] Sketch006
  FullyConstrained = true
  Placement = pos=(13,0,0) rot=(0.57735,0.57735,0.57735;2.0944rad)
  sketch-geometry (8):
    g0: LineSegment StartX=-4.99878 StartY=-6.1818 StartZ=0 EndX=4.63409 EndY=5.7308 EndZ=0
    g1: LineSegment StartX=0 StartY=0 StartZ=0 EndX=-2.33276 EndY=1.88633 EndZ=0
    g2: Circle CenterX=4.63409 CenterY=5.7308 CenterZ=0 NormalX=0 NormalY=0 NormalZ=1 AngleXU=0 Radius=1
    g3: Circle CenterX=-2.33276 CenterY=1.88633 CenterZ=0 NormalX=0 NormalY=0 NormalZ=1 AngleXU=0 Radius=1
    g4: Circle CenterX=-4.99878 CenterY=-6.1818 CenterZ=0 NormalX=0 NormalY=0 NormalZ=1 AngleXU=0 Radius=1
    g5: BSplineCurve PolesCount=3 KnotsCount=2 Degree=2 IsPeriodic=0
    g6: GeomPoint X=4.63409 Y=5.7308 Z=0
    g7: GeomPoint X=-4.99878 Y=-6.1818 Z=0
  constraints (18):
    c: PointOnObject(g-1,g0)
    c: Distance(g-1,g0) = 7.37
    c: Distance(g-1,g0) = 7.95
    c: Angle(g0,g-1) = 2.25078
    c: Coincident(g1,g-1)
    c: Angle(g1,g0) = 1.5708
    c: Distance(g1) = 3
    c: Weight(g2) = 1
    c: Coincident(g5,g0)
    c: Equal(g2,g3)
    c: Coincident(g3,g1)
    c: Equal(g2,g4)
    c: Coincident(g5,g0)
    c: InternalAlignment(g2,g5)
    c: InternalAlignment(g3,g5)
    c: InternalAlignment(g4,g5)
    c: InternalAlignment(g6,g5)
    c: InternalAlignment(g7,g5)
FEATURE [Part::Loft] Loft
  Closed = false
  MaxDegree = 5
  Ruled = false
  Sections = -> [Sketch004,Sketch005]
  Solid = true
FEATURE [Part::Loft] Loft001
  Closed = false
  MaxDegree = 5
  Ruled = true
  Sections = -> [Sketch005,Sketch006,Sketch001]
  Solid = true
FEATURE [Part::Loft] Loft002
  Closed = false
  MaxDegree = 5
  Ruled = false
  Sections = -> [Sketch001,Sketch002,Sketch003]
  Solid = true
FEATURE [Part::Fuse] Fusion
  Base = -> Loft
  Tool = -> Loft001
FEATURE [Part::Fuse] Fusion001
  Base = -> Loft
  Tool = -> Loft001
FEATURE [Part::Fuse] Fusion002
  Base = -> Fusion
  Tool = -> Loft002
FEATURE [Part::FeaturePython] Clone  label="Fusion003"  # Draft clone (typed FeaturePython)
  AttacherType = Attacher::AttachEngine3D
  Fuse = false
  Objects = -> [Fusion002]
  Placement = pos=(0,0,0) rot=(0,0,1;3.14159rad)
  Scale = (1,1,1)
FEATURE [Part::Fuse] Fusion003  label="Fusion004"
  Base = -> Fusion002
  Tool = -> Clone
FEATURE [PartDesign::FeatureBase] BaseFeature
  BaseFeature = -> Fusion003
FEATURE [Sketcher::SketchObject] Sketch007
  FullyConstrained = true
  sketch-geometry (4):
    g0: ArcOfCircle CenterX=-6 CenterY=0 CenterZ=0 NormalX=0 NormalY=0 NormalZ=1 AngleXU=0 Radius=3 StartAngle=1.5708 EndAngle=4.71239
    g1: ArcOfCircle CenterX=6 CenterY=0 CenterZ=0 NormalX=0 NormalY=0 NormalZ=1 AngleXU=0 Radius=3 StartAngle=4.71239 EndAngle=7.85398
    g2: LineSegment StartX=-6 StartY=-3 StartZ=0 EndX=6 EndY=-3 EndZ=0
    g3: LineSegment StartX=6 StartY=3 StartZ=0 EndX=-6 EndY=3 EndZ=0
  constraints (9):
    c: Tangent(g0,g2) = -1.5708
    c: Tangent(g2,g1) = -1.5708
    c: Tangent(g1,g3) = -1.5708
    c: Tangent(g3,g0) = -1.5708
    c: Equal(g0,g1)
    c: PointOnObject(g0,g-1)
    c: Symmetric(g0,g1,g-2)
    c: DistanceY(g1,g1) = 6
    c: DistanceX(g0,g1) = 12
FEATURE [PartDesign::Pad] Pad
  BaseFeature = -> BaseFeature
  Direction = (0,0,1)
  Length = 8
  Length2 = 10
  Midplane = true
  Profile = -> Sketch007
  ReferenceAxis = -> Sketch007 [N_Axis]
  Type = 0
FEATURE [Sketcher::SketchObject] Sketch008
  FullyConstrained = true
  MapMode = 5
  Placement = pos=(0,0,-4) rot=(1,0,0;3.14159rad)
  Support = -> [Pad]
  sketch-geometry (1):
    g0: Circle CenterX=0 CenterY=0 CenterZ=0 NormalX=0 NormalY=0 NormalZ=1 AngleXU=0 Radius=8
  constraints (2):
    c: Coincident(g0,g-1)
    c: Diameter(g0) = 16
FEATURE [PartDesign::Point] DatumPoint
  AttacherType = Attacher::AttachEnginePoint
  AttachmentOffset = pos=(0,0,-3) rot=(0,0,1;0rad)
  MapMode = 37
  Placement = pos=(-2e-16,-1e-16,-7) rot=(0,0,1;0rad)
  Support = -> [Pad]
FEATURE [PartDesign::Plane] DatumPlane
  Length = 154.613
  MapMode = 1
  Placement = pos=(-2e-16,-1e-16,-7) rot=(0,0,1;0rad)
  ResizeMode = 0
  Support = -> [DatumPoint]
  Width = 66.6132
FEATURE [Sketcher::SketchObject] Sketch009
  FullyConstrained = true
  MapMode = 5
  Placement = pos=(-2e-16,-1e-16,-7) rot=(0,0,1;0rad)
  Support = -> [DatumPlane]
  sketch-geometry (1):
    g0: Circle CenterX=0 CenterY=0 CenterZ=0 NormalX=0 NormalY=0 NormalZ=1 AngleXU=0 Radius=9
  constraints (2):
    c: Coincident(g0,g-1)
    c: Diameter(g0) = 18
FEATURE [PartDesign::AdditiveLoft] AdditiveLoft
  BaseFeature = -> Pad
  Closed = false
  Profile = -> Sketch008
  Ruled = false
  Sections = -> [Sketch009]
FEATURE [Sketcher::SketchObject] Sketch010
  FullyConstrained = true
  MapMode = 5
  Placement = pos=(0,0,-4) rot=(0,0,1;0rad)
  Support = -> [AdditiveLoft]
  sketch-geometry (2):
    g0: Circle CenterX=0 CenterY=5.5 CenterZ=0 NormalX=0 NormalY=0 NormalZ=1 AngleXU=0 Radius=1
    g1: Circle CenterX=0 CenterY=-5.5 CenterZ=0 NormalX=0 NormalY=0 NormalZ=1 AngleXU=0 Radius=1
  constraints (5):
    c: PointOnObject(g0,g-2)
    c: Equal(g1,g0)
    c: Diameter(g0) = 2
    c: DistanceY(g1,g0) = 11
    c: Symmetric(g1,g0,g-1)
FEATURE [PartDesign::Pocket] Pocket
  BaseFeature = -> AdditiveLoft
  Direction = (0,0,-1)
  Length = 5
  Length2 = 5
  Profile = -> Sketch010
  ReferenceAxis = -> Sketch010 [N_Axis]
  Type = 1
FEATURE [Sketcher::SketchObject] Sketch011
  ExternalGeometry = -> [Pocket]
  FullyConstrained = true
  MapMode = 5
  Placement = pos=(0,0,-7) rot=(1,0,0;3.14159rad)
  Support = -> [Pocket]
  sketch-geometry (2):
    g0: Circle CenterX=0 CenterY=0 CenterZ=0 NormalX=0 NormalY=0 NormalZ=1 AngleXU=0 Radius=9
    g1: Circle CenterX=0 CenterY=0 CenterZ=0 NormalX=0 NormalY=0 NormalZ=1 AngleXU=0 Radius=8.2
  constraints (4):
    c: Coincident(g0,g-3)
    c: Equal(g0,g-3)
    c: Coincident(g1,g0)
    c: Diameter(g1) = 16.4
FEATURE [PartDesign::Pad] Pad001
  BaseFeature = -> Pocket
  Direction = (0,0,-1)
  Length = 1
  Length2 = 10
  Profile = -> Sketch011
  ReferenceAxis = -> Sketch011 [N_Axis]
  Type = 0
FEATURE [PartDesign::CoordinateSystem] LCS_1
  AttacherType = Attacher::AttachEngine3D
  MapMode = 11
  Placement = pos=(-1.8e-15,0,-7) rot=(0.707107,-0.707107,0;3.14159rad)
  Support = -> [Pad001]
FEATURE [PartDesign::Body] Body
  BaseFeature = -> Fusion003
  Group = -> [BaseFeature,Sketch,Sketch001,Sketch002,Sketch003,Sketch004,Sketch005,Sketch006,Sketch007,Pad,Sketch008,DatumPoint,DatumPlane,Sketch009,AdditiveLoft,Sketch010,Pocket,Sketch011,Pad001,LCS_1]
  Origin = -> Origin
  Tip = -> Pad001
---- part prop1.FCStd = doc fcstd_44143f55c429 ----
FCSTD DOCUMENT  (FreeCAD 0.20R29410 (Git))
Label: prop1
License: All rights reserved
LicenseURL: http://en.wikipedia.org/wiki/All_rights_reserved
objects: Sketcher::SketchObject×12, Part::Fuse×4, Part::Loft×3, PartDesign::FeatureBase×2, PartDesign::Pad×2, PartDesign::Body×2, Part::FeaturePython×1, PartDesign::Point×1, PartDesign::Plane×1, PartDesign::AdditiveLoft×1, PartDesign::Pocket×1, Part::Mirroring×1, PartDesign::CoordinateSystem×1
note: 36 computed .brp shape members not serialized (recipe doc carries the construction recipe); baked Part::Feature solids carry a one-line shape summary decoded from their .brp

FEATURE [Sketcher::SketchObject] Sketch
  FullyConstrained = true
  MapMode = 5
  Support = -> [XY_Plane]
  sketch-geometry (38):
    g0: LineSegment StartX=0 StartY=-3 StartZ=0 EndX=0 EndY=3 EndZ=0
    g1: LineSegment StartX=0 StartY=3 StartZ=0 EndX=9 EndY=3 EndZ=0
    g2: LineSegment StartX=0 StartY=-3 StartZ=0 EndX=9 EndY=-3 EndZ=0
    g3: LineSegment StartX=9 StartY=3 StartZ=0 EndX=19 EndY=7 EndZ=0
    g4: LineSegment StartX=19 StartY=7 StartZ=0 EndX=69 EndY=3 EndZ=0
    g5: LineSegment StartX=69 StartY=3 StartZ=0 EndX=69 EndY=-5 EndZ=0
    g6: LineSegment StartX=9 StartY=-3 StartZ=0 EndX=13 EndY=-5 EndZ=0
    g7: LineSegment StartX=13 StartY=-5 StartZ=0 EndX=18 EndY=-12 EndZ=0
    g8: LineSegment StartX=18 StartY=-12 StartZ=0 EndX=69 EndY=-5 EndZ=0
    g9: GeomPoint X=5 Y=0 Z=0
    g10: GeomPoint X=10 Y=0 Z=0
    g11: GeomPoint X=15 Y=0 Z=0
    g12: GeomPoint X=20 Y=0 Z=0
    g13: GeomPoint X=25 Y=0 Z=0
    g14: GeomPoint X=30 Y=0 Z=0
    g15: GeomPoint X=35 Y=0 Z=0
    g16: GeomPoint X=40 Y=0 Z=0
    g17: GeomPoint X=45 Y=0 Z=0
    g18: GeomPoint X=50 Y=0 Z=0
    g19: GeomPoint X=55 Y=0 Z=0
    g20: GeomPoint X=60 Y=0 Z=0
    g21: GeomPoint X=65 Y=0 Z=0
    g22: GeomPoint X=69 Y=0 Z=0
    g23: LineSegment StartX=0 StartY=16.18 StartZ=0 EndX=32.3915 EndY=-10.0247 EndZ=0
    g24: ArcOfCircle CenterX=20 CenterY=0 CenterZ=0 NormalX=0 NormalY=0 NormalZ=1 AngleXU=0 Radius=6.92 StartAngle=1.5708 EndAngle=3.14159
    g25: LineSegment StartX=13.08 StartY=8e-16 StartZ=0 EndX=13.08 EndY=5.59828 EndZ=0
    g26: ArcOfCircle CenterX=20 CenterY=0 CenterZ=0 NormalX=0 NormalY=0 NormalZ=1 AngleXU=0 Radius=11.7255 StartAngle=4.71239 EndAngle=6.28319
    g27: LineSegment StartX=31.7255 StartY=-2.9e-15 StartZ=0 EndX=31.7255 EndY=-9.48592 EndZ=0
    g28: LineSegment StartX=0 StartY=16.18 StartZ=0 EndX=87.6232 EndY=-4.367 EndZ=0
    g29: ArcOfCircle CenterX=69 CenterY=0 CenterZ=0 NormalX=0 NormalY=0 NormalZ=1 AngleXU=0 Radius=3 StartAngle=1.5708 EndAngle=3.14159
    g30: ArcOfCircle CenterX=69 CenterY=0 CenterZ=0 NormalX=0 NormalY=0 NormalZ=1 AngleXU=0 Radius=5 StartAngle=4.71239 EndAngle=6.28319
    g31: LineSegment StartX=66 StartY=4e-16 StartZ=0 EndX=66 EndY=0.703478 EndZ=0
    g32: LineSegment StartX=74 StartY=-1.2e-15 StartZ=0 EndX=74 EndY=-1.17246 EndZ=0
    g33: LineSegment StartX=0 StartY=16.18 StartZ=0 EndX=22.3034 EndY=-11.4093 EndZ=0
    g34: ArcOfCircle CenterX=13.08 CenterY=8e-16 CenterZ=0 NormalX=0 NormalY=0 NormalZ=1 AngleXU=0 Radius=4.632 StartAngle=1.5708 EndAngle=3.14159
    g35: ArcOfCircle CenterX=13.08 CenterY=8e-16 CenterZ=0 NormalX=0 NormalY=0 NormalZ=1 AngleXU=0 Radius=5.00064 StartAngle=4.69639 EndAngle=6.28319
    g36: LineSegment StartX=8.448 StartY=1.4e-15 StartZ=0 EndX=8.448 EndY=5.7298 EndZ=0
    g37: LineSegment StartX=18.0806 StartY=-4e-16 StartZ=0 EndX=18.0806 EndY=-6.18581 EndZ=0
  constraints (103):
    c: PointOnObject(g0,g-2)
    c: DistanceY(g0,g0) = 6
    c: Symmetric(g0,g0,g-1)
    c: Coincident(g1,g0)
    c: Horizontal(g1)
    c: Coincident(g2,g0)
    c: Horizontal(g2)
    c: Equal(g2,g1)
    c: DistanceX(g1,g1) = 9
    c: Coincident(g3,g1)
    c: DistanceX(g1,g3) = 10
    c: DistanceY(g1,g3) = 4
    c: Coincident(g4,g3)
    c: DistanceX(g3,g4) = 50
    c: DistanceY(g4,g3) = 4
    c: Coincident(g5,g4)
    c: Vertical(g5)
    c: DistanceY(g5,g5) = 8
    c: Coincident(g6,g2)
    c: DistanceY(g6,g2) = 2
    c: DistanceX(g2,g6) = 4
    c: Coincident(g7,g6)
    c: DistanceX(g6,g7) = 5
    c: DistanceY(g7,g6) = 7
    c: Coincident(g8,g7)
    c: Coincident(g8,g5)
    c: PointOnObject(g9,g-1)
    c: DistanceX(g-1,g9) = 5
    c: PointOnObject(g10,g-1)
    c: PointOnObject(g11,g-1)
    c: PointOnObject(g12,g-1)
    c: PointOnObject(g13,g-1)
    c: DistanceX(g10) = 10
    c: DistanceX(g11) = 15
    c: DistanceX(g12) = 20
    c: DistanceX(g13) = 25
    c: PointOnObject(g14,g-1)
    c: PointOnObject(g15,g-1)
    c: PointOnObject(g16,g-1)
    c: PointOnObject(g17,g-1)
    c: PointOnObject(g18,g-1)
    c: PointOnObject(g19,g-1)
    c: DistanceX(g14) = 30
    c: DistanceX(g15) = 35
    c: DistanceX(g16) = 40
    c: DistanceX(g17) = 45
    c: DistanceX(g18) = 50
    c: DistanceX(g19) = 55
    c: PointOnObject(g20,g-1)
    c: PointOnObject(g21,g-1)
    c: PointOnObject(g22,g5)
    c: PointOnObject(g22,g-1)
    c: DistanceX(g20) = 60
    c: DistanceX(g21) = 65
    c: PointOnObject(g23,g-2)
    c: DistanceY(g23) = 16.18
    c: PointOnObject(g12,g23)
    c: Coincident(g24,g12)
    c: PointOnObject(g24,g4)
    c: PointOnObject(g24,g-1)
    c: Coincident(g25,g24)
    c: PointOnObject(g25,g23)
    c: Vertical(g25)
    c: Vertical(g24,g12)
    c: PointOnObject(g23,g8)
    c: Coincident(g26,g12)
    c: PointOnObject(g26,g8)
    c: PointOnObject(g26,g-1)
    c: Vertical(g26,g12)
    c: Coincident(g27,g26)
    c: Vertical(g27)
    c: PointOnObject(g27,g23)
    c: Coincident(g28,g23)
    c: PointOnObject(g22,g28)
    c: Distance(g28) = 90
    c: Coincident(g29,g22)
    c: Coincident(g29,g4)
    c: PointOnObject(g29,g-1)
    c: Coincident(g30,g22)
    c: Coincident(g30,g5)
    c: PointOnObject(g30,g-1)
    c: Coincident(g31,g29)
    c: PointOnObject(g31,g28)
    c: Vertical(g31)
    c: Coincident(g32,g30)
    c: PointOnObject(g32,g28)
    c: Vertical(g32)
    c: Coincident(g33,g23)
    c: PointOnObject(g33,g8)
    c: PointOnObject(g24,g33)
    c: Coincident(g34,g24)
    c: PointOnObject(g34,g3)
    c: PointOnObject(g34,g-1)
    c: Coincident(g35,g24)
    c: Coincident(g35,g6)
    c: PointOnObject(g35,g-1)
    c: Vertical(g34,g24)
    c: Coincident(g36,g34)
    c: PointOnObject(g36,g33)
    c: Vertical(g36)
    c: Coincident(g37,g35)
    c: PointOnObject(g37,g33)
    c: Vertical(g37)
FEATURE [Sketcher::SketchObject] Sketch001
  FullyConstrained = true
  Placement = pos=(20,0,0) rot=(0.57735,0.57735,0.57735;2.0944rad)
  sketch-geometry (8):
    g0: LineSegment StartX=-11.7243 StartY=-9.48401 StartZ=0 EndX=6.91953 EndY=5.59733 EndZ=0
    g1: LineSegment StartX=0 StartY=0 StartZ=0 EndX=-1.88674 EndY=2.33243 EndZ=0
    g2: Circle CenterX=-11.7243 CenterY=-9.48401 CenterZ=0 NormalX=0 NormalY=0 NormalZ=1 AngleXU=0 Radius=1
    g3: Circle CenterX=-1.88674 CenterY=2.33243 CenterZ=0 NormalX=0 NormalY=0 NormalZ=1 AngleXU=0 Radius=1
    g4: Circle CenterX=6.91953 CenterY=5.59733 CenterZ=0 NormalX=0 NormalY=0 NormalZ=1 AngleXU=0 Radius=1
    g5: BSplineCurve PolesCount=3 KnotsCount=2 Degree=2 IsPeriodic=0
    g6: GeomPoint X=-11.7243 Y=-9.48401 Z=0
    g7: GeomPoint X=6.91953 Y=5.59733 Z=0
  constraints (18):
    c: PointOnObject(g-1,g0)
    c: Distance(g-1,g0) = 8.9
    c: Distance(g-1,g0) = 15.08
    c: Angle(g0,g-1) = 2.46144
    c: Coincident(g1,g-1)
    c: Distance(g1) = 3
    c: Angle(g1,g0) = 1.5708
    c: Weight(g2) = 1
    c: Coincident(g5,g0)
    c: Equal(g2,g3)
    c: Coincident(g3,g1)
    c: Equal(g2,g4)
    c: Coincident(g5,g0)
    c: InternalAlignment(g2,g5)
    c: InternalAlignment(g3,g5)
    c: InternalAlignment(g4,g5)
    c: InternalAlignment(g6,g5)
    c: InternalAlignment(g7,g5)
FEATURE [Sketcher::SketchObject] Sketch002
  FullyConstrained = true
  Placement = pos=(50,0,0) rot=(0.57735,0.57735,0.57735;2.0944rad)
  sketch-geometry (8):
    g0: LineSegment StartX=-7.60195 StartY=-2.45976 StartZ=0 EndX=4.51931 EndY=1.46231 EndZ=0
    g1: LineSegment StartX=0 StartY=0 StartZ=0 EndX=-0.923564 EndY=2.8543 EndZ=0
    g2: Circle CenterX=4.51931 CenterY=1.46231 CenterZ=0 NormalX=0 NormalY=0 NormalZ=1 AngleXU=0 Radius=1
    g3: Circle CenterX=-0.923564 CenterY=2.8543 CenterZ=0 NormalX=0 NormalY=0 NormalZ=1 AngleXU=0 Radius=1
    g4: Circle CenterX=-7.60195 CenterY=-2.45976 CenterZ=0 NormalX=0 NormalY=0 NormalZ=1 AngleXU=0 Radius=1
    g5: BSplineCurve PolesCount=3 KnotsCount=2 Degree=2 IsPeriodic=0
    g6: GeomPoint X=4.51931 Y=1.46231 Z=0
    g7: GeomPoint X=-7.60195 Y=-2.45976 Z=0
  constraints (18):
    c: PointOnObject(g-1,g0)
    c: Distance(g-1,g0) = 4.75
    c: Distance(g-1,g0) = 7.99
    c: Angle(g0,g-1) = 2.82866
    c: Coincident(g1,g-1)
    c: Angle(g1,g0) = 1.5708
    c: Distance(g1) = 3
    c: Weight(g2) = 1
    c: Coincident(g5,g0)
    c: Equal(g2,g3)
    c: Coincident(g3,g1)
    c: Equal(g2,g4)
    c: Coincident(g5,g0)
    c: InternalAlignment(g2,g5)
    c: InternalAlignment(g3,g5)
    c: InternalAlignment(g4,g5)
    c: InternalAlignment(g6,g5)
    c: InternalAlignment(g7,g5)
FEATURE [Sketcher::SketchObject] Sketch003
  FullyConstrained = true
  Placement = pos=(69,0,0) rot=(0.57735,0.57735,0.57735;2.0944rad)
  sketch-geometry (8):
    g0: LineSegment StartX=-4.99466 StartY=-1.17057 StartZ=0 EndX=2.99875 EndY=0.702797 EndZ=0
    g1: LineSegment StartX=0 StartY=0 StartZ=0 EndX=-0.684543 EndY=2.92086 EndZ=0
    g2: Circle CenterX=2.99875 CenterY=0.702797 CenterZ=0 NormalX=0 NormalY=0 NormalZ=1 AngleXU=0 Radius=1
    g3: Circle CenterX=-0.684543 CenterY=2.92086 CenterZ=0 NormalX=0 NormalY=0 NormalZ=1 AngleXU=0 Radius=1
    g4: Circle CenterX=-4.99466 CenterY=-1.17057 CenterZ=0 NormalX=0 NormalY=0 NormalZ=1 AngleXU=0 Radius=1
    g5: BSplineCurve PolesCount=3 KnotsCount=2 Degree=2 IsPeriodic=0
    g6: GeomPoint X=2.99875 Y=0.702797 Z=0
    g7: GeomPoint X=-4.99466 Y=-1.17057 Z=0
  constraints (18):
    c: PointOnObject(g-1,g0)
    c: Angle(g0,g-1) = 2.91138
    c: Coincident(g1,g-1)
    c: Angle(g1,g0) = 1.5708
    c: Distance(g1) = 3
    c: Distance(g1,g0) = 3.08
    c: Distance(g1,g0) = 5.13
    c: Weight(g2) = 1
    c: Coincident(g5,g0)
    c: Equal(g2,g3)
    c: Coincident(g3,g1)
    c: Equal(g2,g4)
    c: Coincident(g5,g0)
    c: InternalAlignment(g2,g5)
    c: InternalAlignment(g3,g5)
    c: InternalAlignment(g4,g5)
    c: InternalAlignment(g6,g5)
    c: InternalAlignment(g7,g5)
FEATURE [Sketcher::SketchObject] Sketch004
  FullyConstrained = true
  Placement = pos=(0,0,0) rot=(0.57735,0.57735,0.57735;2.0944rad)
  sketch-geometry (4):
    g0: ArcOfCircle CenterX=-1 CenterY=0 CenterZ=0 NormalX=0 NormalY=0 NormalZ=1 AngleXU=0 Radius=2 StartAngle=1.5708 EndAngle=4.71239
    g1: ArcOfCircle CenterX=1 CenterY=0 CenterZ=0 NormalX=0 NormalY=0 NormalZ=1 AngleXU=0 Radius=2 StartAngle=4.71239 EndAngle=7.85398
    g2: LineSegment StartX=-1 StartY=-2 StartZ=0 EndX=1 EndY=-2 EndZ=0
    g3: LineSegment StartX=1 StartY=2 StartZ=0 EndX=-1 EndY=2 EndZ=0
  constraints (9):
    c: Tangent(g0,g2) = -1.5708
    c: Tangent(g2,g1) = -1.5708
    c: Tangent(g1,g3) = -1.5708
    c: Tangent(g3,g0) = -1.5708
    c: Equal(g0,g1)
    c: PointOnObject(g0,g-1)
    c: Symmetric(g0,g1,g-2)
    c: DistanceY(g1,g1) = 4
    c: DistanceX(g0,g1) = 2
FEATURE [Sketcher::SketchObject] Sketch005
  FullyConstrained = true
  Placement = pos=(9,0,0) rot=(0.57735,0.57735,0.57735;2.0944rad)
  sketch-geometry (7):
    g0: Circle CenterX=3 CenterY=0 CenterZ=0 NormalX=0 NormalY=0 NormalZ=1 AngleXU=0 Radius=1
    g1: Circle CenterX=0 CenterY=2 CenterZ=0 NormalX=0 NormalY=0 NormalZ=1 AngleXU=0 Radius=1
    g2: Circle CenterX=-3 CenterY=4e-16 CenterZ=0 NormalX=0 NormalY=0 NormalZ=1 AngleXU=0 Radius=1
    g3: BSplineCurve PolesCount=3 KnotsCount=2 Degree=2 IsPeriodic=0
    g4: GeomPoint X=3 Y=0 Z=0
    g5: GeomPoint X=-3 Y=4e-16 Z=0
    g6: ArcOfCircle CenterX=0 CenterY=4 CenterZ=0 NormalX=0 NormalY=0 NormalZ=1 AngleXU=0 Radius=5 StartAngle=4.06889 EndAngle=5.35589
  constraints (17):
    c: Weight(g0) = 1
    c: PointOnObject(g3,g-1)
    c: Equal(g0,g1)
    c: PointOnObject(g1,g-2)
    c: Equal(g0,g2)
    c: InternalAlignment(g0,g3)
    c: InternalAlignment(g1,g3)
    c: InternalAlignment(g2,g3)
    c: InternalAlignment(g4,g3)
    c: InternalAlignment(g5,g3)
    c: DistanceY(g-1,g1) = 2
    c: PointOnObject(g6,g-2)
    c: Coincident(g6,g3)
    c: Coincident(g6,g3)
    c: PointOnObject(g3,g-1)
    c: DistanceX(g3,g3) = 6
    c: Diameter(g6) = 10
FEATURE [Sketcher::SketchObject] Sketch006
  FullyConstrained = true
  Placement = pos=(13,0,0) rot=(0.57735,0.57735,0.57735;2.0944rad)
  sketch-geometry (8):
    g0: LineSegment StartX=-4.99878 StartY=-6.1818 StartZ=0 EndX=4.63409 EndY=5.7308 EndZ=0
    g1: LineSegment StartX=0 StartY=0 StartZ=0 EndX=-2.33276 EndY=1.88633 EndZ=0
    g2: Circle CenterX=4.63409 CenterY=5.7308 CenterZ=0 NormalX=0 NormalY=0 NormalZ=1 AngleXU=0 Radius=1
    g3: Circle CenterX=-2.33276 CenterY=1.88633 CenterZ=0 NormalX=0 NormalY=0 NormalZ=1 AngleXU=0 Radius=1
    g4: Circle CenterX=-4.99878 CenterY=-6.1818 CenterZ=0 NormalX=0 NormalY=0 NormalZ=1 AngleXU=0 Radius=1
    g5: BSplineCurve PolesCount=3 KnotsCount=2 Degree=2 IsPeriodic=0
    g6: GeomPoint X=4.63409 Y=5.7308 Z=0
    g7: GeomPoint X=-4.99878 Y=-6.1818 Z=0
  constraints (18):
    c: PointOnObject(g-1,g0)
    c: Distance(g-1,g0) = 7.37
    c: Distance(g-1,g0) = 7.95
    c: Angle(g0,g-1) = 2.25078
    c: Coincident(g1,g-1)
    c: Angle(g1,g0) = 1.5708
    c: Distance(g1) = 3
    c: Weight(g2) = 1
    c: Coincident(g5,g0)
    c: Equal(g2,g3)
    c: Coincident(g3,g1)
    c: Equal(g2,g4)
    c: Coincident(g5,g0)
    c: InternalAlignment(g2,g5)
    c: InternalAlignment(g3,g5)
    c: InternalAlignment(g4,g5)
    c: InternalAlignment(g6,g5)
    c: InternalAlignment(g7,g5)
FEATURE [Part::Loft] Loft
  Closed = false
  MaxDegree = 5
  Ruled = false
  Sections = -> [Sketch004,Sketch005]
  Solid = true
FEATURE [Part::Loft] Loft001
  Closed = false
  MaxDegree = 5
  Ruled = true
  Sections = -> [Sketch005,Sketch006,Sketch001]
  Solid = true
FEATURE [Part::Loft] Loft002
  Closed = false
  MaxDegree = 5
  Ruled = false
  Sections = -> [Sketch001,Sketch002,Sketch003]
  Solid = true
FEATURE [Part::Fuse] Fusion
  Base = -> Loft
  Tool = -> Loft001
FEATURE [Part::Fuse] Fusion001
  Base = -> Loft
  Tool = -> Loft001
FEATURE [Part::Fuse] Fusion002
  Base = -> Fusion
  Tool = -> Loft002
FEATURE [Part::FeaturePython] Clone  label="Fusion003"  # Draft clone (typed FeaturePython)
  AttacherType = Attacher::AttachEngine3D
  Fuse = false
  Objects = -> [Fusion002]
  Placement = pos=(0,0,0) rot=(0,0,1;3.14159rad)
  Scale = (1,1,1)
FEATURE [Part::Fuse] Fusion003  label="Fusion004"
  Base = -> Fusion002
  Tool = -> Clone
FEATURE [PartDesign::FeatureBase] BaseFeature
  BaseFeature = -> Fusion003
FEATURE [Sketcher::SketchObject] Sketch007
  FullyConstrained = true
  sketch-geometry (4):
    g0: ArcOfCircle CenterX=-6 CenterY=0 CenterZ=0 NormalX=0 NormalY=0 NormalZ=1 AngleXU=0 Radius=3 StartAngle=1.5708 EndAngle=4.71239
    g1: ArcOfCircle CenterX=6 CenterY=0 CenterZ=0 NormalX=0 NormalY=0 NormalZ=1 AngleXU=0 Radius=3 StartAngle=4.71239 EndAngle=7.85398
    g2: LineSegment StartX=-6 StartY=-3 StartZ=0 EndX=6 EndY=-3 EndZ=0
    g3: LineSegment StartX=6 StartY=3 StartZ=0 EndX=-6 EndY=3 EndZ=0
  constraints (9):
    c: Tangent(g0,g2) = -1.5708
    c: Tangent(g2,g1) = -1.5708
    c: Tangent(g1,g3) = -1.5708
    c: Tangent(g3,g0) = -1.5708
    c: Equal(g0,g1)
    c: PointOnObject(g0,g-1)
    c: Symmetric(g0,g1,g-2)
    c: DistanceY(g1,g1) = 6
    c: DistanceX(g0,g1) = 12
FEATURE [PartDesign::Pad] Pad
  BaseFeature = -> BaseFeature
  Direction = (0,0,1)
  Length = 8
  Length2 = 10
  Midplane = true
  Profile = -> Sketch007
  ReferenceAxis = -> Sketch007 [N_Axis]
  Type = 0
FEATURE [Sketcher::SketchObject] Sketch008
  FullyConstrained = true
  MapMode = 5
  Placement = pos=(0,0,-4) rot=(1,0,0;3.14159rad)
  Support = -> [Pad]
  sketch-geometry (1):
    g0: Circle CenterX=0 CenterY=0 CenterZ=0 NormalX=0 NormalY=0 NormalZ=1 AngleXU=0 Radius=8
  constraints (2):
    c: Coincident(g0,g-1)
    c: Diameter(g0) = 16
FEATURE [PartDesign::Point] DatumPoint
  AttacherType = Attacher::AttachEnginePoint
  AttachmentOffset = pos=(0,0,-3) rot=(0,0,1;0rad)
  MapMode = 37
  Placement = pos=(-2e-16,-1e-16,-7) rot=(0,0,1;0rad)
  Support = -> [Pad]
FEATURE [PartDesign::Plane] DatumPlane
  Length = 60
  MapMode = 1
  Placement = pos=(-2e-16,-1e-16,-7) rot=(0,0,1;0rad)
  ResizeMode = 0
  Support = -> [DatumPoint]
  Width = 60
FEATURE [Sketcher::SketchObject] Sketch009
  FullyConstrained = true
  MapMode = 5
  Placement = pos=(-2e-16,-1e-16,-7) rot=(0,0,1;0rad)
  Support = -> [DatumPlane]
  sketch-geometry (1):
    g0: Circle CenterX=0 CenterY=0 CenterZ=0 NormalX=0 NormalY=0 NormalZ=1 AngleXU=0 Radius=9
  constraints (2):
    c: Coincident(g0,g-1)
    c: Diameter(g0) = 18
FEATURE [PartDesign::AdditiveLoft] AdditiveLoft
  BaseFeature = -> Pad
  Closed = false
  Profile = -> Sketch008
  Ruled = false
  Sections = -> [Sketch009]
FEATURE [Sketcher::SketchObject] Sketch010
  FullyConstrained = true
  MapMode = 5
  Placement = pos=(0,0,-4) rot=(0,0,1;0rad)
  Support = -> [AdditiveLoft]
  sketch-geometry (2):
    g0: Circle CenterX=0 CenterY=5.5 CenterZ=0 NormalX=0 NormalY=0 NormalZ=1 AngleXU=0 Radius=1
    g1: Circle CenterX=0 CenterY=-5.5 CenterZ=0 NormalX=0 NormalY=0 NormalZ=1 AngleXU=0 Radius=1
  constraints (5):
    c: PointOnObject(g0,g-2)
    c: Equal(g1,g0)
    c: Diameter(g0) = 2
    c: DistanceY(g1,g0) = 11
    c: Symmetric(g1,g0,g-1)
FEATURE [PartDesign::Pocket] Pocket
  BaseFeature = -> AdditiveLoft
  Direction = (0,0,-1)
  Length = 5
  Length2 = 5
  Profile = -> Sketch010
  ReferenceAxis = -> Sketch010 [N_Axis]
  Type = 1
FEATURE [Sketcher::SketchObject] Sketch011
  ExternalGeometry = -> [Pocket]
  FullyConstrained = true
  MapMode = 5
  Placement = pos=(0,0,-7) rot=(1,0,0;3.14159rad)
  Support = -> [Pocket]
  sketch-geometry (2):
    g0: Circle CenterX=0 CenterY=0 CenterZ=0 NormalX=0 NormalY=0 NormalZ=1 AngleXU=0 Radius=9
    g1: Circle CenterX=0 CenterY=0 CenterZ=0 NormalX=0 NormalY=0 NormalZ=1 AngleXU=0 Radius=8.2
  constraints (4):
    c: Coincident(g0,g-3)
    c: Equal(g0,g-3)
    c: Coincident(g1,g0)
    c: Diameter(g1) = 16.4
FEATURE [PartDesign::Pad] Pad001
  BaseFeature = -> Pocket
  Direction = (0,0,-1)
  Length = 1
  Length2 = 10
  Profile = -> Sketch011
  ReferenceAxis = -> Sketch011 [N_Axis]
  Type = 0
FEATURE [PartDesign::Body] Body
  BaseFeature = -> Fusion003
  Group = -> [BaseFeature,Sketch,Sketch001,Sketch002,Sketch003,Sketch004,Sketch005,Sketch006,Sketch007,Pad,Sketch008,DatumPoint,DatumPlane,Sketch009,AdditiveLoft,Sketch010,Pocket,Sketch011,Pad001]
  Origin = -> Origin
  Tip = -> Pad001
FEATURE [Part::Mirroring] mirror  label="Body (mirrored) "
  Base = (0,0,0)
  Normal = (1,0,0)
  Source = -> Body
FEATURE [PartDesign::FeatureBase] BaseFeature001
  BaseFeature = -> mirror
FEATURE [PartDesign::CoordinateSystem] LCS_2
  AttacherType = Attacher::AttachEngine3D
  MapMode = 11
  Placement = pos=(1.8e-15,0,-7) rot=(0,0,-1;1.5708rad)
  Support = -> [BaseFeature001]
FEATURE [PartDesign::Body] Body001
  BaseFeature = -> mirror
  Group = -> [BaseFeature001,LCS_2]
  Origin = -> Origin001
  Tip = -> BaseFeature001
---- part top_plate.FCStd = doc fcstd_edde64554fa4 ----
FCSTD DOCUMENT  (FreeCAD 0.20R29410 (Git))
Label: top_plate
License: All rights reserved
LicenseURL: http://en.wikipedia.org/wiki/All_rights_reserved
objects: PartDesign::CoordinateSystem×2, Sketcher::SketchObject×1, PartDesign::Pad×1, PartDesign::Body×1
note: 6 computed .brp shape members not serialized (recipe doc carries the construction recipe); baked Part::Feature solids carry a one-line shape summary decoded from their .brp

FEATURE [Sketcher::SketchObject] Sketch
  FullyConstrained = true
  MapMode = 5
  Support = -> [XY_Plane]
  sketch-geometry (8):
    g0: LineSegment StartX=-17.5 StartY=100 StartZ=0 EndX=17.5 EndY=100 EndZ=0
    g1: LineSegment StartX=17.5 StartY=100 StartZ=0 EndX=17.5 EndY=-100 EndZ=0
    g2: LineSegment StartX=17.5 StartY=-100 StartZ=0 EndX=-17.5 EndY=-100 EndZ=0
    g3: LineSegment StartX=-17.5 StartY=-100 StartZ=0 EndX=-17.5 EndY=100 EndZ=0
    g4: Circle CenterX=-13.5 CenterY=-96 CenterZ=0 NormalX=0 NormalY=0 NormalZ=1 AngleXU=0 Radius=1.55
    g5: Circle CenterX=13.5 CenterY=-96 CenterZ=0 NormalX=0 NormalY=0 NormalZ=1 AngleXU=0 Radius=1.55
    g6: Circle CenterX=-13.5 CenterY=96 CenterZ=0 NormalX=0 NormalY=0 NormalZ=1 AngleXU=0 Radius=1.55
    g7: Circle CenterX=13.5 CenterY=96 CenterZ=0 NormalX=0 NormalY=0 NormalZ=1 AngleXU=0 Radius=1.55
  constraints (20):
    c: Coincident(g0,g1)
    c: Coincident(g1,g2)
    c: Coincident(g2,g3)
    c: Coincident(g3,g0)
    c: Horizontal(g0)
    c: Vertical(g3)
    c: DistanceX(g2,g2) = 35
    c: Symmetric(g2,g1,g-2)
    c: Symmetric(g1,g0,g-1)
    c: DistanceY(g1,g1) = 200
    c: Symmetric(g5,g4,g-2)
    c: Equal(g4,g5)
    c: Diameter(g5) = 3.1
    c: DistanceY(g1,g5) = 4
    c: DistanceX(g5,g1) = 4
    c: Equal(g7,g6)
    c: Symmetric(g7,g6,g-2)
    c: DistanceX(g7,g0) = 4
    c: DistanceY(g7,g0) = 4
    c: Diameter(g7) = 3.1
FEATURE [PartDesign::Pad] Pad
  Direction = (0,0,1)
  Length = 2
  Length2 = 10
  Profile = -> Sketch
  ReferenceAxis = -> Sketch [N_Axis]
  Type = 0
FEATURE [PartDesign::CoordinateSystem] LCS_1
  AttacherType = Attacher::AttachEngine3D
  MapMode = 11
  Placement = pos=(-13.5,96,0) rot=(0,0,1;1.5708rad)
  Support = -> [Pad]
FEATURE [PartDesign::CoordinateSystem] LCS_2
  AttacherType = Attacher::AttachEngine3D
  MapMode = 11
  Placement = pos=(13.5,96,0) rot=(0,0,1;1.5708rad)
  Support = -> [Pad]
FEATURE [PartDesign::Body] Body
  Group = -> [Sketch,Pad,LCS_1,LCS_2]
  Origin = -> Origin
  Tip = -> Pad
